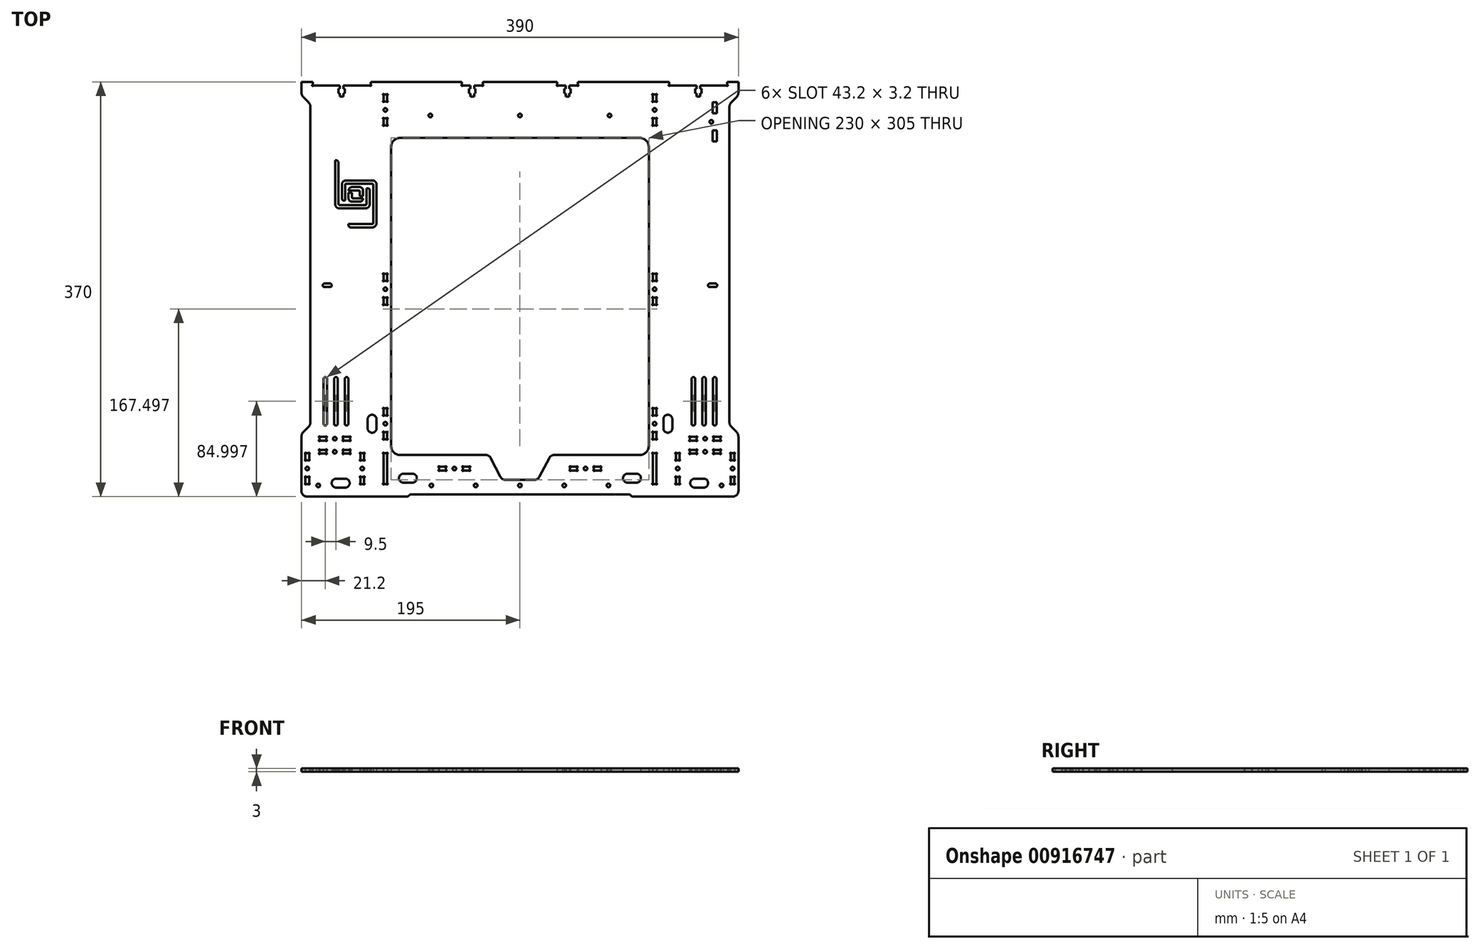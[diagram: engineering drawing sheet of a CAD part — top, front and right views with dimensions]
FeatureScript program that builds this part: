
annotation { "Feature Type Name" : "Feature", "Feature Type Description" : "" }
export const myFeature = defineFeature(function(context is Context, id is Id, definition is map)
    precondition{}
    {
        {
            var Q0;
            Q0=qCreatedBy(makeId("Top.planeOp"),FACE);
            var sketch = newSketch(context, id + "F0", { "sketchPlane" : qUnion([Q0])});
            skCircle(sketch, "E0", {"center": v(-180, -171.15) * mm, "radius": 1.6 * mm});
            skCircle(sketch, "E1", {"center": v(0, 158.85) * mm, "radius": 1.6 * mm});
            skLineSegment(sketch, "E2", {"start": v(-156, -165.15) * mm, "end": v(-164, -165.15) * mm});
            skArc(sketch, "E3", {"start": v(-156, -173.15) * mm, "mid": v(-152, -169.15) * mm, "end": v(-156, -165.15) * mm});
            skLineSegment(sketch, "E4", {"start": v(-164, -173.15) * mm, "end": v(-156, -173.15) * mm});
            skArc(sketch, "E5", {"start": v(-164, -165.15) * mm, "mid": v(-168, -169.15) * mm, "end": v(-164, -173.15) * mm});
            skLineSegment(sketch, "E6", {"start": v(156, -173.15) * mm, "end": v(164, -173.15) * mm});
            skArc(sketch, "E7", {"start": v(156, -165.15) * mm, "mid": v(152, -169.15) * mm, "end": v(156, -173.15) * mm});
            skLineSegment(sketch, "E8", {"start": v(164, -165.15) * mm, "end": v(156, -165.15) * mm});
            skArc(sketch, "E9", {"start": v(164, -173.15) * mm, "mid": v(168, -169.15) * mm, "end": v(164, -165.15) * mm});
            skLineSegment(sketch, "E10", {"start": v(-165.9, -76.15) * mm, "end": v(-165.9, -116.15) * mm});
            skArc(sketch, "E11", {"start": v(-162.7, -76.15) * mm, "mid": v(-164.3, -74.55) * mm, "end": v(-165.9, -76.15) * mm});
            skLineSegment(sketch, "E12", {"start": v(-162.7, -116.15) * mm, "end": v(-162.7, -76.15) * mm});
            skArc(sketch, "E13", {"start": v(-165.9, -116.15) * mm, "mid": v(-164.3, -117.75) * mm, "end": v(-162.7, -116.15) * mm});
            skLineSegment(sketch, "E14", {"start": v(-156.4, -76.15) * mm, "end": v(-156.4, -116.15) * mm});
            skArc(sketch, "E15", {"start": v(-153.2, -76.15) * mm, "mid": v(-154.8, -74.55) * mm, "end": v(-156.4, -76.15) * mm});
            skLineSegment(sketch, "E16", {"start": v(-153.2, -116.15) * mm, "end": v(-153.2, -76.15) * mm});
            skArc(sketch, "E17", {"start": v(-156.4, -116.15) * mm, "mid": v(-154.8, -117.75) * mm, "end": v(-153.2, -116.15) * mm});
            skLineSegment(sketch, "E18", {"start": v(-175.4, -76.15) * mm, "end": v(-175.4, -116.15) * mm});
            skArc(sketch, "E19", {"start": v(-172.2, -76.15) * mm, "mid": v(-173.8, -74.55) * mm, "end": v(-175.4, -76.15) * mm});
            skLineSegment(sketch, "E20", {"start": v(-172.2, -116.15) * mm, "end": v(-172.2, -76.15) * mm});
            skArc(sketch, "E21", {"start": v(-175.4, -116.15) * mm, "mid": v(-173.8, -117.75) * mm, "end": v(-172.2, -116.15) * mm});
            skCircle(sketch, "E22", {"center": v(170.82, 153.25) * mm, "radius": 1.6 * mm});
            skCircle(sketch, "E23", {"center": v(165.3, -141.15) * mm, "radius": 1.6 * mm});
            skLineSegment(sketch, "E24", {"start": v(-157.8, -140.37) * mm, "end": v(-157.8, -141.94) * mm});
            skArc(sketch, "E25", {"start": v(-157.8, -140.37) * mm, "mid": v(-157.87, -140.12) * mm, "end": v(-158.05, -139.94) * mm});
            skArc(sketch, "E26", {"start": v(-157.37, -139.25) * mm, "mid": v(-158.15, -139.15) * mm, "end": v(-158.05, -139.94) * mm});
            skArc(sketch, "E27", {"start": v(-157.37, -139.25) * mm, "mid": v(-157.18, -139.44) * mm, "end": v(-156.93, -139.5) * mm});
            skLineSegment(sketch, "E28", {"start": v(-152.47, -139.5) * mm, "end": v(-156.93, -139.5) * mm});
            skArc(sketch, "E29", {"start": v(-152.47, -139.5) * mm, "mid": v(-152.22, -139.44) * mm, "end": v(-152.03, -139.25) * mm});
            skArc(sketch, "E30", {"start": v(-151.35, -139.94) * mm, "mid": v(-151.25, -139.15) * mm, "end": v(-152.03, -139.25) * mm});
            skArc(sketch, "E31", {"start": v(-151.35, -139.94) * mm, "mid": v(-151.53, -140.12) * mm, "end": v(-151.6, -140.37) * mm});
            skLineSegment(sketch, "E32", {"start": v(-151.6, -141.94) * mm, "end": v(-151.6, -140.37) * mm});
            skArc(sketch, "E33", {"start": v(-151.6, -141.94) * mm, "mid": v(-151.53, -142.19) * mm, "end": v(-151.35, -142.37) * mm});
            skArc(sketch, "E34", {"start": v(-152.03, -143.05) * mm, "mid": v(-151.25, -143.16) * mm, "end": v(-151.35, -142.37) * mm});
            skArc(sketch, "E35", {"start": v(-152.03, -143.05) * mm, "mid": v(-152.22, -142.87) * mm, "end": v(-152.47, -142.8) * mm});
            skLineSegment(sketch, "E36", {"start": v(-156.93, -142.8) * mm, "end": v(-152.47, -142.8) * mm});
            skArc(sketch, "E37", {"start": v(-156.93, -142.8) * mm, "mid": v(-157.18, -142.87) * mm, "end": v(-157.37, -143.05) * mm});
            skArc(sketch, "E38", {"start": v(-158.05, -142.37) * mm, "mid": v(-158.15, -143.16) * mm, "end": v(-157.37, -143.05) * mm});
            skArc(sketch, "E39", {"start": v(-158.05, -142.37) * mm, "mid": v(-157.87, -142.19) * mm, "end": v(-157.8, -141.94) * mm});
            skLineSegment(sketch, "E40", {"start": v(-179, -140.37) * mm, "end": v(-179, -141.94) * mm});
            skArc(sketch, "E41", {"start": v(-179, -140.37) * mm, "mid": v(-179.07, -140.12) * mm, "end": v(-179.25, -139.94) * mm});
            skArc(sketch, "E42", {"start": v(-178.57, -139.25) * mm, "mid": v(-179.35, -139.15) * mm, "end": v(-179.25, -139.94) * mm});
            skArc(sketch, "E43", {"start": v(-178.57, -139.25) * mm, "mid": v(-178.38, -139.44) * mm, "end": v(-178.13, -139.5) * mm});
            skLineSegment(sketch, "E44", {"start": v(-173.67, -139.5) * mm, "end": v(-178.13, -139.5) * mm});
            skArc(sketch, "E45", {"start": v(-173.67, -139.5) * mm, "mid": v(-173.42, -139.44) * mm, "end": v(-173.23, -139.25) * mm});
            skArc(sketch, "E46", {"start": v(-172.55, -139.94) * mm, "mid": v(-172.45, -139.15) * mm, "end": v(-173.23, -139.25) * mm});
            skArc(sketch, "E47", {"start": v(-172.55, -139.94) * mm, "mid": v(-172.73, -140.12) * mm, "end": v(-172.8, -140.37) * mm});
            skLineSegment(sketch, "E48", {"start": v(-172.8, -141.94) * mm, "end": v(-172.8, -140.37) * mm});
            skArc(sketch, "E49", {"start": v(-172.8, -141.94) * mm, "mid": v(-172.73, -142.19) * mm, "end": v(-172.55, -142.37) * mm});
            skArc(sketch, "E50", {"start": v(-173.23, -143.05) * mm, "mid": v(-172.45, -143.16) * mm, "end": v(-172.55, -142.37) * mm});
            skArc(sketch, "E51", {"start": v(-173.23, -143.05) * mm, "mid": v(-173.42, -142.87) * mm, "end": v(-173.67, -142.8) * mm});
            skLineSegment(sketch, "E52", {"start": v(-178.13, -142.8) * mm, "end": v(-173.67, -142.8) * mm});
            skArc(sketch, "E53", {"start": v(-178.13, -142.8) * mm, "mid": v(-178.38, -142.87) * mm, "end": v(-178.57, -143.05) * mm});
            skArc(sketch, "E54", {"start": v(-179.25, -142.37) * mm, "mid": v(-179.35, -143.16) * mm, "end": v(-178.57, -143.05) * mm});
            skArc(sketch, "E55", {"start": v(-179.25, -142.37) * mm, "mid": v(-179.07, -142.19) * mm, "end": v(-179, -141.94) * mm});
            skLineSegment(sketch, "E56", {"start": v(-96, -160.75) * mm, "end": v(-104, -160.75) * mm});
            skArc(sketch, "E57", {"start": v(-96, -168.75) * mm, "mid": v(-92, -164.75) * mm, "end": v(-96, -160.75) * mm});
            skLineSegment(sketch, "E58", {"start": v(-104, -168.75) * mm, "end": v(-96, -168.75) * mm});
            skArc(sketch, "E59", {"start": v(-104, -160.75) * mm, "mid": v(-108, -164.75) * mm, "end": v(-104, -168.75) * mm});
            skLineSegment(sketch, "E60", {"start": v(104, -160.75) * mm, "end": v(96, -160.75) * mm});
            skArc(sketch, "E61", {"start": v(104, -168.75) * mm, "mid": v(108, -164.75) * mm, "end": v(104, -160.75) * mm});
            skLineSegment(sketch, "E62", {"start": v(96, -168.75) * mm, "end": v(104, -168.75) * mm});
            skArc(sketch, "E63", {"start": v(96, -160.75) * mm, "mid": v(92, -164.75) * mm, "end": v(96, -168.75) * mm});
            skCircle(sketch, "E64", {"center": v(-79.02, -171.15) * mm, "radius": 1.6 * mm});
            skCircle(sketch, "E65", {"center": v(39.5, -171.15) * mm, "radius": 1.6 * mm});
            skCircle(sketch, "E66", {"center": v(58.53, -156.15) * mm, "radius": 1.6 * mm});
            skLineSegment(sketch, "E67", {"start": v(-51.03, -155.37) * mm, "end": v(-51.03, -156.94) * mm});
            skArc(sketch, "E68", {"start": v(-51.03, -155.37) * mm, "mid": v(-51.1, -155.12) * mm, "end": v(-51.28, -154.94) * mm});
            skArc(sketch, "E69", {"start": v(-50.6, -154.25) * mm, "mid": v(-51.38, -154.15) * mm, "end": v(-51.28, -154.94) * mm});
            skArc(sketch, "E70", {"start": v(-50.6, -154.25) * mm, "mid": v(-50.4, -154.44) * mm, "end": v(-50.16, -154.5) * mm});
            skLineSegment(sketch, "E71", {"start": v(-45.7, -154.5) * mm, "end": v(-50.16, -154.5) * mm});
            skArc(sketch, "E72", {"start": v(-45.7, -154.5) * mm, "mid": v(-45.44, -154.44) * mm, "end": v(-45.26, -154.25) * mm});
            skArc(sketch, "E73", {"start": v(-44.58, -154.94) * mm, "mid": v(-44.47, -154.15) * mm, "end": v(-45.26, -154.25) * mm});
            skArc(sketch, "E74", {"start": v(-44.58, -154.94) * mm, "mid": v(-44.76, -155.12) * mm, "end": v(-44.83, -155.37) * mm});
            skLineSegment(sketch, "E75", {"start": v(-44.83, -156.94) * mm, "end": v(-44.83, -155.37) * mm});
            skArc(sketch, "E76", {"start": v(-44.83, -156.94) * mm, "mid": v(-44.76, -157.19) * mm, "end": v(-44.58, -157.37) * mm});
            skArc(sketch, "E77", {"start": v(-45.26, -158.05) * mm, "mid": v(-44.47, -158.16) * mm, "end": v(-44.58, -157.37) * mm});
            skArc(sketch, "E78", {"start": v(-45.26, -158.05) * mm, "mid": v(-45.44, -157.87) * mm, "end": v(-45.7, -157.8) * mm});
            skLineSegment(sketch, "E79", {"start": v(-50.16, -157.8) * mm, "end": v(-45.7, -157.8) * mm});
            skArc(sketch, "E80", {"start": v(-50.16, -157.8) * mm, "mid": v(-50.4, -157.87) * mm, "end": v(-50.6, -158.05) * mm});
            skArc(sketch, "E81", {"start": v(-51.28, -157.37) * mm, "mid": v(-51.38, -158.16) * mm, "end": v(-50.6, -158.05) * mm});
            skArc(sketch, "E82", {"start": v(-51.28, -157.37) * mm, "mid": v(-51.1, -157.19) * mm, "end": v(-51.03, -156.94) * mm});
            skLineSegment(sketch, "E83", {"start": v(-72.23, -155.37) * mm, "end": v(-72.23, -156.94) * mm});
            skArc(sketch, "E84", {"start": v(-72.23, -155.37) * mm, "mid": v(-72.3, -155.12) * mm, "end": v(-72.48, -154.94) * mm});
            skArc(sketch, "E85", {"start": v(-71.8, -154.25) * mm, "mid": v(-72.58, -154.15) * mm, "end": v(-72.48, -154.94) * mm});
            skArc(sketch, "E86", {"start": v(-71.8, -154.25) * mm, "mid": v(-71.6, -154.44) * mm, "end": v(-71.36, -154.5) * mm});
            skLineSegment(sketch, "E87", {"start": v(-66.9, -154.5) * mm, "end": v(-71.36, -154.5) * mm});
            skArc(sketch, "E88", {"start": v(-66.9, -154.5) * mm, "mid": v(-66.64, -154.44) * mm, "end": v(-66.46, -154.25) * mm});
            skArc(sketch, "E89", {"start": v(-65.78, -154.94) * mm, "mid": v(-65.67, -154.15) * mm, "end": v(-66.46, -154.25) * mm});
            skArc(sketch, "E90", {"start": v(-65.78, -154.94) * mm, "mid": v(-65.96, -155.12) * mm, "end": v(-66.03, -155.37) * mm});
            skLineSegment(sketch, "E91", {"start": v(-66.03, -156.94) * mm, "end": v(-66.03, -155.37) * mm});
            skArc(sketch, "E92", {"start": v(-66.03, -156.94) * mm, "mid": v(-65.96, -157.19) * mm, "end": v(-65.78, -157.37) * mm});
            skArc(sketch, "E93", {"start": v(-66.46, -158.05) * mm, "mid": v(-65.67, -158.16) * mm, "end": v(-65.78, -157.37) * mm});
            skArc(sketch, "E94", {"start": v(-66.46, -158.05) * mm, "mid": v(-66.64, -157.87) * mm, "end": v(-66.9, -157.8) * mm});
            skLineSegment(sketch, "E95", {"start": v(-71.36, -157.8) * mm, "end": v(-66.9, -157.8) * mm});
            skArc(sketch, "E96", {"start": v(-71.36, -157.8) * mm, "mid": v(-71.6, -157.87) * mm, "end": v(-71.8, -158.05) * mm});
            skArc(sketch, "E97", {"start": v(-72.48, -157.37) * mm, "mid": v(-72.58, -158.16) * mm, "end": v(-71.8, -158.05) * mm});
            skArc(sketch, "E98", {"start": v(-72.48, -157.37) * mm, "mid": v(-72.3, -157.19) * mm, "end": v(-72.23, -156.94) * mm});
            skCircle(sketch, "E99", {"center": v(189.82, -156.15) * mm, "radius": 1.6 * mm});
            skCircle(sketch, "E100", {"center": v(140.78, -156.15) * mm, "radius": 1.6 * mm});
            skCircle(sketch, "E101", {"center": v(120.17, 3.85) * mm, "radius": 1.6 * mm});
            skCircle(sketch, "E102", {"center": v(-120.18, 163.85) * mm, "radius": 1.6 * mm});
            skCircle(sketch, "E103", {"center": v(-120.17, -116.15) * mm, "radius": 1.6 * mm});
            skCircle(sketch, "E104", {"center": v(-165.3, -129.5) * mm, "radius": 1.6 * mm});
            skArc(sketch, "E105", {"start": v(188.17, -143.32) * mm, "mid": v(188.1, -143.07) * mm, "end": v(187.92, -142.89) * mm});
            skArc(sketch, "E106", {"start": v(188.6, -142.2) * mm, "mid": v(187.82, -142.1) * mm, "end": v(187.92, -142.89) * mm});
            skArc(sketch, "E107", {"start": v(188.6, -142.2) * mm, "mid": v(188.79, -142.39) * mm, "end": v(189.04, -142.45) * mm});
            skLineSegment(sketch, "E108", {"start": v(190.6, -142.45) * mm, "end": v(189.04, -142.45) * mm});
            skArc(sketch, "E109", {"start": v(190.6, -142.45) * mm, "mid": v(190.85, -142.39) * mm, "end": v(191.04, -142.2) * mm});
            skArc(sketch, "E110", {"start": v(191.72, -142.89) * mm, "mid": v(191.82, -142.1) * mm, "end": v(191.04, -142.2) * mm});
            skArc(sketch, "E111", {"start": v(191.72, -142.89) * mm, "mid": v(191.54, -143.07) * mm, "end": v(191.47, -143.32) * mm});
            skLineSegment(sketch, "E112", {"start": v(191.47, -147.79) * mm, "end": v(191.47, -143.32) * mm});
            skArc(sketch, "E113", {"start": v(191.47, -147.79) * mm, "mid": v(191.54, -148.04) * mm, "end": v(191.72, -148.22) * mm});
            skArc(sketch, "E114", {"start": v(191.04, -148.9) * mm, "mid": v(191.82, -149) * mm, "end": v(191.72, -148.22) * mm});
            skArc(sketch, "E115", {"start": v(191.04, -148.9) * mm, "mid": v(190.85, -148.72) * mm, "end": v(190.6, -148.65) * mm});
            skLineSegment(sketch, "E116", {"start": v(189.04, -148.65) * mm, "end": v(190.6, -148.65) * mm});
            skArc(sketch, "E117", {"start": v(189.04, -148.65) * mm, "mid": v(188.79, -148.72) * mm, "end": v(188.6, -148.9) * mm});
            skArc(sketch, "E118", {"start": v(187.92, -148.22) * mm, "mid": v(187.82, -149) * mm, "end": v(188.6, -148.9) * mm});
            skArc(sketch, "E119", {"start": v(187.92, -148.22) * mm, "mid": v(188.1, -148.04) * mm, "end": v(188.17, -147.79) * mm});
            skLineSegment(sketch, "E120", {"start": v(188.17, -143.32) * mm, "end": v(188.17, -147.79) * mm});
            skArc(sketch, "E121", {"start": v(188.17, -164.52) * mm, "mid": v(188.1, -164.27) * mm, "end": v(187.92, -164.09) * mm});
            skArc(sketch, "E122", {"start": v(188.6, -163.4) * mm, "mid": v(187.82, -163.3) * mm, "end": v(187.92, -164.09) * mm});
            skArc(sketch, "E123", {"start": v(188.6, -163.4) * mm, "mid": v(188.79, -163.59) * mm, "end": v(189.04, -163.65) * mm});
            skLineSegment(sketch, "E124", {"start": v(190.6, -163.65) * mm, "end": v(189.04, -163.65) * mm});
            skArc(sketch, "E125", {"start": v(190.6, -163.65) * mm, "mid": v(190.85, -163.59) * mm, "end": v(191.04, -163.4) * mm});
            skArc(sketch, "E126", {"start": v(191.72, -164.09) * mm, "mid": v(191.82, -163.3) * mm, "end": v(191.04, -163.4) * mm});
            skArc(sketch, "E127", {"start": v(191.72, -164.09) * mm, "mid": v(191.54, -164.27) * mm, "end": v(191.47, -164.52) * mm});
            skLineSegment(sketch, "E128", {"start": v(191.47, -168.99) * mm, "end": v(191.47, -164.52) * mm});
            skArc(sketch, "E129", {"start": v(191.47, -168.99) * mm, "mid": v(191.54, -169.24) * mm, "end": v(191.72, -169.42) * mm});
            skArc(sketch, "E130", {"start": v(191.04, -170.1) * mm, "mid": v(191.82, -170.2) * mm, "end": v(191.72, -169.42) * mm});
            skArc(sketch, "E131", {"start": v(191.04, -170.1) * mm, "mid": v(190.85, -169.92) * mm, "end": v(190.6, -169.85) * mm});
            skLineSegment(sketch, "E132", {"start": v(189.04, -169.85) * mm, "end": v(190.6, -169.85) * mm});
            skArc(sketch, "E133", {"start": v(189.04, -169.85) * mm, "mid": v(188.79, -169.92) * mm, "end": v(188.6, -170.1) * mm});
            skArc(sketch, "E134", {"start": v(187.92, -169.42) * mm, "mid": v(187.82, -170.2) * mm, "end": v(188.6, -170.1) * mm});
            skArc(sketch, "E135", {"start": v(187.92, -169.42) * mm, "mid": v(188.1, -169.24) * mm, "end": v(188.17, -168.99) * mm});
            skLineSegment(sketch, "E136", {"start": v(188.17, -164.52) * mm, "end": v(188.17, -168.99) * mm});
            skArc(sketch, "E137", {"start": v(178.13, -127.86) * mm, "mid": v(178.38, -127.8) * mm, "end": v(178.57, -127.6) * mm});
            skArc(sketch, "E138", {"start": v(179.25, -128.3) * mm, "mid": v(179.35, -127.5) * mm, "end": v(178.57, -127.6) * mm});
            skArc(sketch, "E139", {"start": v(179.25, -128.3) * mm, "mid": v(179.07, -128.47) * mm, "end": v(179, -128.72) * mm});
            skLineSegment(sketch, "E140", {"start": v(179, -130.3) * mm, "end": v(179, -128.72) * mm});
            skArc(sketch, "E141", {"start": v(179, -130.3) * mm, "mid": v(179.07, -130.54) * mm, "end": v(179.25, -130.72) * mm});
            skArc(sketch, "E142", {"start": v(178.57, -131.4) * mm, "mid": v(179.35, -131.51) * mm, "end": v(179.25, -130.72) * mm});
            skArc(sketch, "E143", {"start": v(178.57, -131.4) * mm, "mid": v(178.38, -131.22) * mm, "end": v(178.13, -131.16) * mm});
            skLineSegment(sketch, "E144", {"start": v(173.67, -131.16) * mm, "end": v(178.13, -131.16) * mm});
            skArc(sketch, "E145", {"start": v(173.67, -131.16) * mm, "mid": v(173.42, -131.22) * mm, "end": v(173.23, -131.4) * mm});
            skArc(sketch, "E146", {"start": v(172.55, -130.72) * mm, "mid": v(172.45, -131.51) * mm, "end": v(173.23, -131.4) * mm});
            skArc(sketch, "E147", {"start": v(172.55, -130.72) * mm, "mid": v(172.73, -130.54) * mm, "end": v(172.8, -130.3) * mm});
            skLineSegment(sketch, "E148", {"start": v(172.8, -128.72) * mm, "end": v(172.8, -130.3) * mm});
            skArc(sketch, "E149", {"start": v(172.8, -128.72) * mm, "mid": v(172.73, -128.47) * mm, "end": v(172.55, -128.3) * mm});
            skArc(sketch, "E150", {"start": v(173.23, -127.6) * mm, "mid": v(172.45, -127.5) * mm, "end": v(172.55, -128.3) * mm});
            skArc(sketch, "E151", {"start": v(173.23, -127.6) * mm, "mid": v(173.42, -127.8) * mm, "end": v(173.67, -127.86) * mm});
            skLineSegment(sketch, "E152", {"start": v(178.13, -127.86) * mm, "end": v(173.67, -127.86) * mm});
            skArc(sketch, "E153", {"start": v(156.93, -127.86) * mm, "mid": v(157.18, -127.8) * mm, "end": v(157.37, -127.6) * mm});
            skArc(sketch, "E154", {"start": v(158.05, -128.3) * mm, "mid": v(158.15, -127.5) * mm, "end": v(157.37, -127.6) * mm});
            skArc(sketch, "E155", {"start": v(158.05, -128.3) * mm, "mid": v(157.87, -128.47) * mm, "end": v(157.8, -128.72) * mm});
            skLineSegment(sketch, "E156", {"start": v(157.8, -130.3) * mm, "end": v(157.8, -128.72) * mm});
            skArc(sketch, "E157", {"start": v(157.8, -130.3) * mm, "mid": v(157.87, -130.54) * mm, "end": v(158.05, -130.72) * mm});
            skArc(sketch, "E158", {"start": v(157.37, -131.4) * mm, "mid": v(158.15, -131.51) * mm, "end": v(158.05, -130.72) * mm});
            skArc(sketch, "E159", {"start": v(157.37, -131.4) * mm, "mid": v(157.18, -131.22) * mm, "end": v(156.93, -131.16) * mm});
            skLineSegment(sketch, "E160", {"start": v(152.47, -131.16) * mm, "end": v(156.93, -131.16) * mm});
            skArc(sketch, "E161", {"start": v(152.47, -131.16) * mm, "mid": v(152.22, -131.22) * mm, "end": v(152.03, -131.4) * mm});
            skArc(sketch, "E162", {"start": v(151.35, -130.72) * mm, "mid": v(151.25, -131.51) * mm, "end": v(152.03, -131.4) * mm});
            skArc(sketch, "E163", {"start": v(151.35, -130.72) * mm, "mid": v(151.53, -130.54) * mm, "end": v(151.6, -130.3) * mm});
            skLineSegment(sketch, "E164", {"start": v(151.6, -128.72) * mm, "end": v(151.6, -130.3) * mm});
            skArc(sketch, "E165", {"start": v(151.6, -128.72) * mm, "mid": v(151.53, -128.47) * mm, "end": v(151.35, -128.3) * mm});
            skArc(sketch, "E166", {"start": v(152.03, -127.6) * mm, "mid": v(151.25, -127.5) * mm, "end": v(151.35, -128.3) * mm});
            skArc(sketch, "E167", {"start": v(152.03, -127.6) * mm, "mid": v(152.22, -127.8) * mm, "end": v(152.47, -127.86) * mm});
            skLineSegment(sketch, "E168", {"start": v(156.93, -127.86) * mm, "end": v(152.47, -127.86) * mm});
            skArc(sketch, "E169", {"start": v(139.13, -143.32) * mm, "mid": v(139.06, -143.07) * mm, "end": v(138.88, -142.89) * mm});
            skArc(sketch, "E170", {"start": v(139.56, -142.2) * mm, "mid": v(138.78, -142.1) * mm, "end": v(138.88, -142.89) * mm});
            skArc(sketch, "E171", {"start": v(139.56, -142.2) * mm, "mid": v(139.75, -142.39) * mm, "end": v(140, -142.45) * mm});
            skLineSegment(sketch, "E172", {"start": v(141.56, -142.45) * mm, "end": v(140, -142.45) * mm});
            skArc(sketch, "E173", {"start": v(141.56, -142.45) * mm, "mid": v(141.81, -142.39) * mm, "end": v(142, -142.2) * mm});
            skArc(sketch, "E174", {"start": v(142.68, -142.89) * mm, "mid": v(142.78, -142.1) * mm, "end": v(142, -142.2) * mm});
            skArc(sketch, "E175", {"start": v(142.68, -142.89) * mm, "mid": v(142.5, -143.07) * mm, "end": v(142.43, -143.32) * mm});
            skLineSegment(sketch, "E176", {"start": v(142.43, -147.79) * mm, "end": v(142.43, -143.32) * mm});
            skArc(sketch, "E177", {"start": v(142.43, -147.79) * mm, "mid": v(142.5, -148.04) * mm, "end": v(142.68, -148.22) * mm});
            skArc(sketch, "E178", {"start": v(142, -148.9) * mm, "mid": v(142.78, -149) * mm, "end": v(142.68, -148.22) * mm});
            skArc(sketch, "E179", {"start": v(142, -148.9) * mm, "mid": v(141.81, -148.72) * mm, "end": v(141.56, -148.65) * mm});
            skLineSegment(sketch, "E180", {"start": v(140, -148.65) * mm, "end": v(141.56, -148.65) * mm});
            skArc(sketch, "E181", {"start": v(140, -148.65) * mm, "mid": v(139.75, -148.72) * mm, "end": v(139.56, -148.9) * mm});
            skArc(sketch, "E182", {"start": v(138.88, -148.22) * mm, "mid": v(138.78, -149) * mm, "end": v(139.56, -148.9) * mm});
            skArc(sketch, "E183", {"start": v(138.88, -148.22) * mm, "mid": v(139.06, -148.04) * mm, "end": v(139.13, -147.79) * mm});
            skLineSegment(sketch, "E184", {"start": v(139.13, -143.32) * mm, "end": v(139.13, -147.79) * mm});
            skArc(sketch, "E185", {"start": v(139.13, -164.52) * mm, "mid": v(139.06, -164.27) * mm, "end": v(138.88, -164.09) * mm});
            skArc(sketch, "E186", {"start": v(139.56, -163.4) * mm, "mid": v(138.78, -163.3) * mm, "end": v(138.88, -164.09) * mm});
            skArc(sketch, "E187", {"start": v(139.56, -163.4) * mm, "mid": v(139.75, -163.59) * mm, "end": v(140, -163.65) * mm});
            skLineSegment(sketch, "E188", {"start": v(141.56, -163.65) * mm, "end": v(140, -163.65) * mm});
            skArc(sketch, "E189", {"start": v(141.56, -163.65) * mm, "mid": v(141.81, -163.59) * mm, "end": v(142, -163.4) * mm});
            skArc(sketch, "E190", {"start": v(142.68, -164.09) * mm, "mid": v(142.78, -163.3) * mm, "end": v(142, -163.4) * mm});
            skArc(sketch, "E191", {"start": v(142.68, -164.09) * mm, "mid": v(142.5, -164.27) * mm, "end": v(142.43, -164.52) * mm});
            skLineSegment(sketch, "E192", {"start": v(142.43, -168.99) * mm, "end": v(142.43, -164.52) * mm});
            skArc(sketch, "E193", {"start": v(142.43, -168.99) * mm, "mid": v(142.5, -169.24) * mm, "end": v(142.68, -169.42) * mm});
            skArc(sketch, "E194", {"start": v(142, -170.1) * mm, "mid": v(142.78, -170.2) * mm, "end": v(142.68, -169.42) * mm});
            skArc(sketch, "E195", {"start": v(142, -170.1) * mm, "mid": v(141.81, -169.92) * mm, "end": v(141.56, -169.85) * mm});
            skLineSegment(sketch, "E196", {"start": v(140, -169.85) * mm, "end": v(141.56, -169.85) * mm});
            skArc(sketch, "E197", {"start": v(140, -169.85) * mm, "mid": v(139.75, -169.92) * mm, "end": v(139.56, -170.1) * mm});
            skArc(sketch, "E198", {"start": v(138.88, -169.42) * mm, "mid": v(138.78, -170.2) * mm, "end": v(139.56, -170.1) * mm});
            skArc(sketch, "E199", {"start": v(138.88, -169.42) * mm, "mid": v(139.06, -169.24) * mm, "end": v(139.13, -168.99) * mm});
            skLineSegment(sketch, "E200", {"start": v(139.13, -164.52) * mm, "end": v(139.13, -168.99) * mm});
            skLineSegment(sketch, "E201", {"start": v(120.96, 177.55) * mm, "end": v(119.4, 177.55) * mm});
            skArc(sketch, "E202", {"start": v(120.96, 177.55) * mm, "mid": v(121.2, 177.61) * mm, "end": v(121.4, 177.8) * mm});
            skArc(sketch, "E203", {"start": v(122.07, 177.11) * mm, "mid": v(122.18, 177.9) * mm, "end": v(121.4, 177.8) * mm});
            skArc(sketch, "E204", {"start": v(122.07, 177.11) * mm, "mid": v(121.9, 176.93) * mm, "end": v(121.82, 176.68) * mm});
            skLineSegment(sketch, "E205", {"start": v(121.82, 172.21) * mm, "end": v(121.82, 176.68) * mm});
            skArc(sketch, "E206", {"start": v(121.82, 172.21) * mm, "mid": v(121.9, 171.96) * mm, "end": v(122.07, 171.78) * mm});
            skArc(sketch, "E207", {"start": v(121.4, 171.1) * mm, "mid": v(122.18, 171) * mm, "end": v(122.07, 171.78) * mm});
            skArc(sketch, "E208", {"start": v(121.4, 171.1) * mm, "mid": v(121.2, 171.28) * mm, "end": v(120.96, 171.35) * mm});
            skLineSegment(sketch, "E209", {"start": v(119.4, 171.35) * mm, "end": v(120.96, 171.35) * mm});
            skArc(sketch, "E210", {"start": v(119.4, 171.35) * mm, "mid": v(119.14, 171.28) * mm, "end": v(118.96, 171.1) * mm});
            skArc(sketch, "E211", {"start": v(118.28, 171.78) * mm, "mid": v(118.17, 171) * mm, "end": v(118.96, 171.1) * mm});
            skArc(sketch, "E212", {"start": v(118.28, 171.78) * mm, "mid": v(118.46, 171.96) * mm, "end": v(118.53, 172.21) * mm});
            skLineSegment(sketch, "E213", {"start": v(118.53, 176.68) * mm, "end": v(118.53, 172.21) * mm});
            skArc(sketch, "E214", {"start": v(118.53, 176.68) * mm, "mid": v(118.46, 176.93) * mm, "end": v(118.28, 177.11) * mm});
            skArc(sketch, "E215", {"start": v(118.96, 177.8) * mm, "mid": v(118.17, 177.9) * mm, "end": v(118.28, 177.11) * mm});
            skArc(sketch, "E216", {"start": v(118.96, 177.8) * mm, "mid": v(119.14, 177.61) * mm, "end": v(119.4, 177.55) * mm});
            skLineSegment(sketch, "E217", {"start": v(120.96, 156.35) * mm, "end": v(119.4, 156.35) * mm});
            skArc(sketch, "E218", {"start": v(120.96, 156.35) * mm, "mid": v(121.2, 156.41) * mm, "end": v(121.4, 156.6) * mm});
            skArc(sketch, "E219", {"start": v(122.07, 155.91) * mm, "mid": v(122.18, 156.7) * mm, "end": v(121.4, 156.6) * mm});
            skArc(sketch, "E220", {"start": v(122.07, 155.91) * mm, "mid": v(121.9, 155.73) * mm, "end": v(121.82, 155.48) * mm});
            skLineSegment(sketch, "E221", {"start": v(121.82, 151.01) * mm, "end": v(121.82, 155.48) * mm});
            skArc(sketch, "E222", {"start": v(121.82, 151.01) * mm, "mid": v(121.9, 150.76) * mm, "end": v(122.07, 150.58) * mm});
            skArc(sketch, "E223", {"start": v(121.4, 149.9) * mm, "mid": v(122.18, 149.8) * mm, "end": v(122.07, 150.58) * mm});
            skArc(sketch, "E224", {"start": v(121.4, 149.9) * mm, "mid": v(121.2, 150.08) * mm, "end": v(120.96, 150.15) * mm});
            skLineSegment(sketch, "E225", {"start": v(119.4, 150.15) * mm, "end": v(120.96, 150.15) * mm});
            skArc(sketch, "E226", {"start": v(119.4, 150.15) * mm, "mid": v(119.14, 150.08) * mm, "end": v(118.96, 149.9) * mm});
            skArc(sketch, "E227", {"start": v(118.28, 150.58) * mm, "mid": v(118.17, 149.8) * mm, "end": v(118.96, 149.9) * mm});
            skArc(sketch, "E228", {"start": v(118.28, 150.58) * mm, "mid": v(118.46, 150.76) * mm, "end": v(118.53, 151.01) * mm});
            skLineSegment(sketch, "E229", {"start": v(118.53, 155.48) * mm, "end": v(118.53, 151.01) * mm});
            skArc(sketch, "E230", {"start": v(118.53, 155.48) * mm, "mid": v(118.46, 155.73) * mm, "end": v(118.28, 155.91) * mm});
            skArc(sketch, "E231", {"start": v(118.96, 156.6) * mm, "mid": v(118.17, 156.7) * mm, "end": v(118.28, 155.91) * mm});
            skArc(sketch, "E232", {"start": v(118.96, 156.6) * mm, "mid": v(119.14, 156.41) * mm, "end": v(119.4, 156.35) * mm});
            skLineSegment(sketch, "E233", {"start": v(120.96, 17.55) * mm, "end": v(119.4, 17.55) * mm});
            skArc(sketch, "E234", {"start": v(120.96, 17.55) * mm, "mid": v(121.2, 17.61) * mm, "end": v(121.4, 17.8) * mm});
            skArc(sketch, "E235", {"start": v(122.07, 17.11) * mm, "mid": v(122.18, 17.9) * mm, "end": v(121.4, 17.8) * mm});
            skArc(sketch, "E236", {"start": v(122.07, 17.11) * mm, "mid": v(121.9, 16.93) * mm, "end": v(121.82, 16.68) * mm});
            skLineSegment(sketch, "E237", {"start": v(121.82, 12.21) * mm, "end": v(121.82, 16.68) * mm});
            skArc(sketch, "E238", {"start": v(121.82, 12.21) * mm, "mid": v(121.9, 11.96) * mm, "end": v(122.07, 11.78) * mm});
            skArc(sketch, "E239", {"start": v(121.4, 11.1) * mm, "mid": v(122.18, 11) * mm, "end": v(122.07, 11.78) * mm});
            skArc(sketch, "E240", {"start": v(121.4, 11.1) * mm, "mid": v(121.2, 11.28) * mm, "end": v(120.96, 11.35) * mm});
            skLineSegment(sketch, "E241", {"start": v(119.4, 11.35) * mm, "end": v(120.96, 11.35) * mm});
            skArc(sketch, "E242", {"start": v(119.4, 11.35) * mm, "mid": v(119.14, 11.28) * mm, "end": v(118.96, 11.1) * mm});
            skArc(sketch, "E243", {"start": v(118.28, 11.78) * mm, "mid": v(118.17, 11) * mm, "end": v(118.96, 11.1) * mm});
            skArc(sketch, "E244", {"start": v(118.28, 11.78) * mm, "mid": v(118.46, 11.96) * mm, "end": v(118.53, 12.21) * mm});
            skLineSegment(sketch, "E245", {"start": v(118.53, 16.68) * mm, "end": v(118.53, 12.21) * mm});
            skArc(sketch, "E246", {"start": v(118.53, 16.68) * mm, "mid": v(118.46, 16.93) * mm, "end": v(118.28, 17.11) * mm});
            skArc(sketch, "E247", {"start": v(118.96, 17.8) * mm, "mid": v(118.17, 17.9) * mm, "end": v(118.28, 17.11) * mm});
            skArc(sketch, "E248", {"start": v(118.96, 17.8) * mm, "mid": v(119.14, 17.61) * mm, "end": v(119.4, 17.55) * mm});
            skLineSegment(sketch, "E249", {"start": v(120.96, -3.65) * mm, "end": v(119.4, -3.65) * mm});
            skArc(sketch, "E250", {"start": v(120.96, -3.65) * mm, "mid": v(121.2, -3.59) * mm, "end": v(121.4, -3.4) * mm});
            skArc(sketch, "E251", {"start": v(122.07, -4.09) * mm, "mid": v(122.18, -3.3) * mm, "end": v(121.4, -3.4) * mm});
            skArc(sketch, "E252", {"start": v(122.07, -4.09) * mm, "mid": v(121.9, -4.27) * mm, "end": v(121.82, -4.52) * mm});
            skLineSegment(sketch, "E253", {"start": v(121.82, -8.99) * mm, "end": v(121.82, -4.52) * mm});
            skArc(sketch, "E254", {"start": v(121.82, -8.99) * mm, "mid": v(121.9, -9.24) * mm, "end": v(122.07, -9.42) * mm});
            skArc(sketch, "E255", {"start": v(121.4, -10.1) * mm, "mid": v(122.18, -10.2) * mm, "end": v(122.07, -9.42) * mm});
            skArc(sketch, "E256", {"start": v(121.4, -10.1) * mm, "mid": v(121.2, -9.92) * mm, "end": v(120.96, -9.85) * mm});
            skLineSegment(sketch, "E257", {"start": v(119.4, -9.85) * mm, "end": v(120.96, -9.85) * mm});
            skArc(sketch, "E258", {"start": v(119.4, -9.85) * mm, "mid": v(119.14, -9.92) * mm, "end": v(118.96, -10.1) * mm});
            skArc(sketch, "E259", {"start": v(118.28, -9.42) * mm, "mid": v(118.17, -10.2) * mm, "end": v(118.96, -10.1) * mm});
            skArc(sketch, "E260", {"start": v(118.28, -9.42) * mm, "mid": v(118.46, -9.24) * mm, "end": v(118.53, -8.99) * mm});
            skLineSegment(sketch, "E261", {"start": v(118.53, -4.52) * mm, "end": v(118.53, -8.99) * mm});
            skArc(sketch, "E262", {"start": v(118.53, -4.52) * mm, "mid": v(118.46, -4.27) * mm, "end": v(118.28, -4.09) * mm});
            skArc(sketch, "E263", {"start": v(118.96, -3.4) * mm, "mid": v(118.17, -3.3) * mm, "end": v(118.28, -4.09) * mm});
            skArc(sketch, "E264", {"start": v(118.96, -3.4) * mm, "mid": v(119.14, -3.59) * mm, "end": v(119.4, -3.65) * mm});
            skArc(sketch, "E265", {"start": v(118.53, -103.32) * mm, "mid": v(118.46, -103.07) * mm, "end": v(118.28, -102.89) * mm});
            skArc(sketch, "E266", {"start": v(118.96, -102.2) * mm, "mid": v(118.17, -102.1) * mm, "end": v(118.28, -102.89) * mm});
            skArc(sketch, "E267", {"start": v(118.96, -102.2) * mm, "mid": v(119.14, -102.39) * mm, "end": v(119.4, -102.45) * mm});
            skLineSegment(sketch, "E268", {"start": v(120.96, -102.45) * mm, "end": v(119.4, -102.45) * mm});
            skArc(sketch, "E269", {"start": v(120.96, -102.45) * mm, "mid": v(121.2, -102.39) * mm, "end": v(121.4, -102.2) * mm});
            skArc(sketch, "E270", {"start": v(122.07, -102.89) * mm, "mid": v(122.18, -102.1) * mm, "end": v(121.4, -102.2) * mm});
            skArc(sketch, "E271", {"start": v(122.07, -102.89) * mm, "mid": v(121.9, -103.07) * mm, "end": v(121.83, -103.32) * mm});
            skLineSegment(sketch, "E272", {"start": v(121.83, -107.79) * mm, "end": v(121.83, -103.32) * mm});
            skArc(sketch, "E273", {"start": v(121.83, -107.79) * mm, "mid": v(121.9, -108.04) * mm, "end": v(122.08, -108.22) * mm});
            skArc(sketch, "E274", {"start": v(121.4, -108.9) * mm, "mid": v(122.18, -109) * mm, "end": v(122.08, -108.22) * mm});
            skArc(sketch, "E275", {"start": v(121.4, -108.9) * mm, "mid": v(121.2, -108.72) * mm, "end": v(120.96, -108.65) * mm});
            skLineSegment(sketch, "E276", {"start": v(119.4, -108.65) * mm, "end": v(120.96, -108.65) * mm});
            skArc(sketch, "E277", {"start": v(119.4, -108.65) * mm, "mid": v(119.14, -108.72) * mm, "end": v(118.96, -108.9) * mm});
            skArc(sketch, "E278", {"start": v(118.28, -108.22) * mm, "mid": v(118.17, -109) * mm, "end": v(118.96, -108.9) * mm});
            skArc(sketch, "E279", {"start": v(118.28, -108.22) * mm, "mid": v(118.46, -108.04) * mm, "end": v(118.53, -107.79) * mm});
            skLineSegment(sketch, "E280", {"start": v(118.53, -103.32) * mm, "end": v(118.53, -107.79) * mm});
            skArc(sketch, "E281", {"start": v(118.53, -124.52) * mm, "mid": v(118.46, -124.27) * mm, "end": v(118.28, -124.09) * mm});
            skArc(sketch, "E282", {"start": v(118.96, -123.4) * mm, "mid": v(118.17, -123.3) * mm, "end": v(118.28, -124.09) * mm});
            skArc(sketch, "E283", {"start": v(118.96, -123.4) * mm, "mid": v(119.14, -123.59) * mm, "end": v(119.4, -123.65) * mm});
            skLineSegment(sketch, "E284", {"start": v(120.96, -123.65) * mm, "end": v(119.4, -123.65) * mm});
            skArc(sketch, "E285", {"start": v(120.96, -123.65) * mm, "mid": v(121.2, -123.59) * mm, "end": v(121.4, -123.4) * mm});
            skArc(sketch, "E286", {"start": v(122.07, -124.09) * mm, "mid": v(122.18, -123.3) * mm, "end": v(121.4, -123.4) * mm});
            skArc(sketch, "E287", {"start": v(122.07, -124.09) * mm, "mid": v(121.9, -124.27) * mm, "end": v(121.83, -124.52) * mm});
            skLineSegment(sketch, "E288", {"start": v(121.83, -128.99) * mm, "end": v(121.83, -124.52) * mm});
            skArc(sketch, "E289", {"start": v(121.83, -128.99) * mm, "mid": v(121.9, -129.24) * mm, "end": v(122.08, -129.42) * mm});
            skArc(sketch, "E290", {"start": v(121.4, -130.1) * mm, "mid": v(122.18, -130.2) * mm, "end": v(122.08, -129.42) * mm});
            skArc(sketch, "E291", {"start": v(121.4, -130.1) * mm, "mid": v(121.2, -129.92) * mm, "end": v(120.96, -129.85) * mm});
            skLineSegment(sketch, "E292", {"start": v(119.4, -129.85) * mm, "end": v(120.96, -129.85) * mm});
            skArc(sketch, "E293", {"start": v(119.4, -129.85) * mm, "mid": v(119.14, -129.92) * mm, "end": v(118.96, -130.1) * mm});
            skArc(sketch, "E294", {"start": v(118.28, -129.42) * mm, "mid": v(118.17, -130.2) * mm, "end": v(118.96, -130.1) * mm});
            skArc(sketch, "E295", {"start": v(118.28, -129.42) * mm, "mid": v(118.46, -129.24) * mm, "end": v(118.53, -128.99) * mm});
            skLineSegment(sketch, "E296", {"start": v(118.53, -124.52) * mm, "end": v(118.53, -128.99) * mm});
            skLineSegment(sketch, "E297", {"start": v(-119.4, 177.55) * mm, "end": v(-120.96, 177.55) * mm});
            skArc(sketch, "E298", {"start": v(-119.4, 177.55) * mm, "mid": v(-119.14, 177.61) * mm, "end": v(-118.96, 177.8) * mm});
            skArc(sketch, "E299", {"start": v(-118.28, 177.11) * mm, "mid": v(-118.17, 177.9) * mm, "end": v(-118.96, 177.8) * mm});
            skArc(sketch, "E300", {"start": v(-118.28, 177.11) * mm, "mid": v(-118.46, 176.93) * mm, "end": v(-118.53, 176.68) * mm});
            skLineSegment(sketch, "E301", {"start": v(-118.53, 172.21) * mm, "end": v(-118.53, 176.68) * mm});
            skArc(sketch, "E302", {"start": v(-118.53, 172.21) * mm, "mid": v(-118.46, 171.96) * mm, "end": v(-118.28, 171.78) * mm});
            skArc(sketch, "E303", {"start": v(-118.96, 171.1) * mm, "mid": v(-118.17, 171) * mm, "end": v(-118.28, 171.78) * mm});
            skArc(sketch, "E304", {"start": v(-118.96, 171.1) * mm, "mid": v(-119.14, 171.28) * mm, "end": v(-119.4, 171.35) * mm});
            skLineSegment(sketch, "E305", {"start": v(-120.96, 171.35) * mm, "end": v(-119.4, 171.35) * mm});
            skArc(sketch, "E306", {"start": v(-120.96, 171.35) * mm, "mid": v(-121.2, 171.28) * mm, "end": v(-121.4, 171.1) * mm});
            skArc(sketch, "E307", {"start": v(-122.07, 171.78) * mm, "mid": v(-122.18, 171) * mm, "end": v(-121.4, 171.1) * mm});
            skArc(sketch, "E308", {"start": v(-122.07, 171.78) * mm, "mid": v(-121.9, 171.96) * mm, "end": v(-121.82, 172.21) * mm});
            skLineSegment(sketch, "E309", {"start": v(-121.82, 176.68) * mm, "end": v(-121.82, 172.21) * mm});
            skArc(sketch, "E310", {"start": v(-121.82, 176.68) * mm, "mid": v(-121.9, 176.93) * mm, "end": v(-122.07, 177.11) * mm});
            skArc(sketch, "E311", {"start": v(-121.4, 177.8) * mm, "mid": v(-122.18, 177.9) * mm, "end": v(-122.07, 177.11) * mm});
            skArc(sketch, "E312", {"start": v(-121.4, 177.8) * mm, "mid": v(-121.2, 177.61) * mm, "end": v(-120.96, 177.55) * mm});
            skLineSegment(sketch, "E313", {"start": v(-119.4, 156.35) * mm, "end": v(-120.96, 156.35) * mm});
            skArc(sketch, "E314", {"start": v(-119.4, 156.35) * mm, "mid": v(-119.14, 156.41) * mm, "end": v(-118.96, 156.6) * mm});
            skArc(sketch, "E315", {"start": v(-118.28, 155.91) * mm, "mid": v(-118.17, 156.7) * mm, "end": v(-118.96, 156.6) * mm});
            skArc(sketch, "E316", {"start": v(-118.28, 155.91) * mm, "mid": v(-118.46, 155.73) * mm, "end": v(-118.53, 155.48) * mm});
            skLineSegment(sketch, "E317", {"start": v(-118.53, 151.01) * mm, "end": v(-118.53, 155.48) * mm});
            skArc(sketch, "E318", {"start": v(-118.53, 151.01) * mm, "mid": v(-118.46, 150.76) * mm, "end": v(-118.28, 150.58) * mm});
            skArc(sketch, "E319", {"start": v(-118.96, 149.9) * mm, "mid": v(-118.17, 149.8) * mm, "end": v(-118.28, 150.58) * mm});
            skArc(sketch, "E320", {"start": v(-118.96, 149.9) * mm, "mid": v(-119.14, 150.08) * mm, "end": v(-119.4, 150.15) * mm});
            skLineSegment(sketch, "E321", {"start": v(-120.96, 150.15) * mm, "end": v(-119.4, 150.15) * mm});
            skArc(sketch, "E322", {"start": v(-120.96, 150.15) * mm, "mid": v(-121.2, 150.08) * mm, "end": v(-121.4, 149.9) * mm});
            skArc(sketch, "E323", {"start": v(-122.07, 150.58) * mm, "mid": v(-122.18, 149.8) * mm, "end": v(-121.4, 149.9) * mm});
            skArc(sketch, "E324", {"start": v(-122.07, 150.58) * mm, "mid": v(-121.9, 150.76) * mm, "end": v(-121.82, 151.01) * mm});
            skLineSegment(sketch, "E325", {"start": v(-121.82, 155.48) * mm, "end": v(-121.82, 151.01) * mm});
            skArc(sketch, "E326", {"start": v(-121.82, 155.48) * mm, "mid": v(-121.9, 155.73) * mm, "end": v(-122.07, 155.91) * mm});
            skArc(sketch, "E327", {"start": v(-121.4, 156.6) * mm, "mid": v(-122.18, 156.7) * mm, "end": v(-122.07, 155.91) * mm});
            skArc(sketch, "E328", {"start": v(-121.4, 156.6) * mm, "mid": v(-121.2, 156.41) * mm, "end": v(-120.96, 156.35) * mm});
            skLineSegment(sketch, "E329", {"start": v(-119.4, 17.55) * mm, "end": v(-120.96, 17.55) * mm});
            skArc(sketch, "E330", {"start": v(-119.4, 17.55) * mm, "mid": v(-119.14, 17.61) * mm, "end": v(-118.96, 17.8) * mm});
            skArc(sketch, "E331", {"start": v(-118.28, 17.11) * mm, "mid": v(-118.17, 17.9) * mm, "end": v(-118.96, 17.8) * mm});
            skArc(sketch, "E332", {"start": v(-118.28, 17.11) * mm, "mid": v(-118.46, 16.93) * mm, "end": v(-118.53, 16.68) * mm});
            skLineSegment(sketch, "E333", {"start": v(-118.53, 12.21) * mm, "end": v(-118.53, 16.68) * mm});
            skArc(sketch, "E334", {"start": v(-118.53, 12.21) * mm, "mid": v(-118.46, 11.96) * mm, "end": v(-118.28, 11.78) * mm});
            skArc(sketch, "E335", {"start": v(-118.96, 11.1) * mm, "mid": v(-118.17, 11) * mm, "end": v(-118.28, 11.78) * mm});
            skArc(sketch, "E336", {"start": v(-118.96, 11.1) * mm, "mid": v(-119.14, 11.28) * mm, "end": v(-119.4, 11.35) * mm});
            skLineSegment(sketch, "E337", {"start": v(-120.96, 11.35) * mm, "end": v(-119.4, 11.35) * mm});
            skArc(sketch, "E338", {"start": v(-120.96, 11.35) * mm, "mid": v(-121.2, 11.28) * mm, "end": v(-121.4, 11.1) * mm});
            skArc(sketch, "E339", {"start": v(-122.07, 11.78) * mm, "mid": v(-122.18, 11) * mm, "end": v(-121.4, 11.1) * mm});
            skArc(sketch, "E340", {"start": v(-122.07, 11.78) * mm, "mid": v(-121.9, 11.96) * mm, "end": v(-121.82, 12.21) * mm});
            skLineSegment(sketch, "E341", {"start": v(-121.82, 16.68) * mm, "end": v(-121.82, 12.21) * mm});
            skArc(sketch, "E342", {"start": v(-121.82, 16.68) * mm, "mid": v(-121.9, 16.93) * mm, "end": v(-122.07, 17.11) * mm});
            skArc(sketch, "E343", {"start": v(-121.4, 17.8) * mm, "mid": v(-122.18, 17.9) * mm, "end": v(-122.07, 17.11) * mm});
            skArc(sketch, "E344", {"start": v(-121.4, 17.8) * mm, "mid": v(-121.2, 17.61) * mm, "end": v(-120.96, 17.55) * mm});
            skLineSegment(sketch, "E345", {"start": v(-119.4, -3.65) * mm, "end": v(-120.96, -3.65) * mm});
            skArc(sketch, "E346", {"start": v(-119.4, -3.65) * mm, "mid": v(-119.14, -3.59) * mm, "end": v(-118.96, -3.4) * mm});
            skArc(sketch, "E347", {"start": v(-118.28, -4.09) * mm, "mid": v(-118.17, -3.3) * mm, "end": v(-118.96, -3.4) * mm});
            skArc(sketch, "E348", {"start": v(-118.28, -4.09) * mm, "mid": v(-118.46, -4.27) * mm, "end": v(-118.53, -4.52) * mm});
            skLineSegment(sketch, "E349", {"start": v(-118.53, -8.99) * mm, "end": v(-118.53, -4.52) * mm});
            skArc(sketch, "E350", {"start": v(-118.53, -8.99) * mm, "mid": v(-118.46, -9.24) * mm, "end": v(-118.28, -9.42) * mm});
            skArc(sketch, "E351", {"start": v(-118.96, -10.1) * mm, "mid": v(-118.17, -10.2) * mm, "end": v(-118.28, -9.42) * mm});
            skArc(sketch, "E352", {"start": v(-118.96, -10.1) * mm, "mid": v(-119.14, -9.92) * mm, "end": v(-119.4, -9.85) * mm});
            skLineSegment(sketch, "E353", {"start": v(-120.96, -9.85) * mm, "end": v(-119.4, -9.85) * mm});
            skArc(sketch, "E354", {"start": v(-120.96, -9.85) * mm, "mid": v(-121.2, -9.92) * mm, "end": v(-121.4, -10.1) * mm});
            skArc(sketch, "E355", {"start": v(-122.07, -9.42) * mm, "mid": v(-122.18, -10.2) * mm, "end": v(-121.4, -10.1) * mm});
            skArc(sketch, "E356", {"start": v(-122.07, -9.42) * mm, "mid": v(-121.9, -9.24) * mm, "end": v(-121.82, -8.99) * mm});
            skLineSegment(sketch, "E357", {"start": v(-121.82, -4.52) * mm, "end": v(-121.82, -8.99) * mm});
            skArc(sketch, "E358", {"start": v(-121.82, -4.52) * mm, "mid": v(-121.9, -4.27) * mm, "end": v(-122.07, -4.09) * mm});
            skArc(sketch, "E359", {"start": v(-121.4, -3.4) * mm, "mid": v(-122.18, -3.3) * mm, "end": v(-122.07, -4.09) * mm});
            skArc(sketch, "E360", {"start": v(-121.4, -3.4) * mm, "mid": v(-121.2, -3.59) * mm, "end": v(-120.96, -3.65) * mm});
            skArc(sketch, "E361", {"start": v(-121.82, -103.32) * mm, "mid": v(-121.9, -103.07) * mm, "end": v(-122.07, -102.89) * mm});
            skArc(sketch, "E362", {"start": v(-121.4, -102.2) * mm, "mid": v(-122.18, -102.1) * mm, "end": v(-122.07, -102.89) * mm});
            skArc(sketch, "E363", {"start": v(-121.4, -102.2) * mm, "mid": v(-121.2, -102.39) * mm, "end": v(-120.96, -102.45) * mm});
            skLineSegment(sketch, "E364", {"start": v(-119.4, -102.45) * mm, "end": v(-120.96, -102.45) * mm});
            skArc(sketch, "E365", {"start": v(-119.4, -102.45) * mm, "mid": v(-119.14, -102.39) * mm, "end": v(-118.96, -102.2) * mm});
            skArc(sketch, "E366", {"start": v(-118.28, -102.89) * mm, "mid": v(-118.17, -102.1) * mm, "end": v(-118.96, -102.2) * mm});
            skArc(sketch, "E367", {"start": v(-118.28, -102.89) * mm, "mid": v(-118.46, -103.07) * mm, "end": v(-118.53, -103.32) * mm});
            skLineSegment(sketch, "E368", {"start": v(-118.52, -107.79) * mm, "end": v(-118.53, -103.32) * mm});
            skArc(sketch, "E369", {"start": v(-118.52, -107.79) * mm, "mid": v(-118.46, -108.04) * mm, "end": v(-118.27, -108.22) * mm});
            skArc(sketch, "E370", {"start": v(-118.96, -108.9) * mm, "mid": v(-118.17, -109) * mm, "end": v(-118.27, -108.22) * mm});
            skArc(sketch, "E371", {"start": v(-118.96, -108.9) * mm, "mid": v(-119.14, -108.72) * mm, "end": v(-119.4, -108.65) * mm});
            skLineSegment(sketch, "E372", {"start": v(-120.96, -108.65) * mm, "end": v(-119.4, -108.65) * mm});
            skArc(sketch, "E373", {"start": v(-120.96, -108.65) * mm, "mid": v(-121.2, -108.72) * mm, "end": v(-121.4, -108.9) * mm});
            skArc(sketch, "E374", {"start": v(-122.07, -108.22) * mm, "mid": v(-122.18, -109) * mm, "end": v(-121.4, -108.9) * mm});
            skArc(sketch, "E375", {"start": v(-122.07, -108.22) * mm, "mid": v(-121.9, -108.04) * mm, "end": v(-121.82, -107.79) * mm});
            skLineSegment(sketch, "E376", {"start": v(-121.82, -103.32) * mm, "end": v(-121.82, -107.79) * mm});
            skArc(sketch, "E377", {"start": v(-121.82, -124.52) * mm, "mid": v(-121.9, -124.27) * mm, "end": v(-122.07, -124.09) * mm});
            skArc(sketch, "E378", {"start": v(-121.4, -123.4) * mm, "mid": v(-122.18, -123.3) * mm, "end": v(-122.07, -124.09) * mm});
            skArc(sketch, "E379", {"start": v(-121.4, -123.4) * mm, "mid": v(-121.2, -123.59) * mm, "end": v(-120.96, -123.65) * mm});
            skLineSegment(sketch, "E380", {"start": v(-119.4, -123.65) * mm, "end": v(-120.96, -123.65) * mm});
            skArc(sketch, "E381", {"start": v(-119.4, -123.65) * mm, "mid": v(-119.14, -123.59) * mm, "end": v(-118.96, -123.4) * mm});
            skArc(sketch, "E382", {"start": v(-118.28, -124.09) * mm, "mid": v(-118.17, -123.3) * mm, "end": v(-118.96, -123.4) * mm});
            skArc(sketch, "E383", {"start": v(-118.28, -124.09) * mm, "mid": v(-118.46, -124.27) * mm, "end": v(-118.52, -124.52) * mm});
            skLineSegment(sketch, "E384", {"start": v(-118.52, -128.99) * mm, "end": v(-118.53, -124.52) * mm});
            skArc(sketch, "E385", {"start": v(-118.52, -128.99) * mm, "mid": v(-118.46, -129.24) * mm, "end": v(-118.27, -129.42) * mm});
            skArc(sketch, "E386", {"start": v(-118.96, -130.1) * mm, "mid": v(-118.17, -130.2) * mm, "end": v(-118.27, -129.42) * mm});
            skArc(sketch, "E387", {"start": v(-118.96, -130.1) * mm, "mid": v(-119.14, -129.92) * mm, "end": v(-119.4, -129.85) * mm});
            skLineSegment(sketch, "E388", {"start": v(-120.96, -129.85) * mm, "end": v(-119.4, -129.85) * mm});
            skArc(sketch, "E389", {"start": v(-120.96, -129.85) * mm, "mid": v(-121.2, -129.92) * mm, "end": v(-121.4, -130.1) * mm});
            skArc(sketch, "E390", {"start": v(-122.07, -129.42) * mm, "mid": v(-122.18, -130.2) * mm, "end": v(-121.4, -130.1) * mm});
            skArc(sketch, "E391", {"start": v(-122.07, -129.42) * mm, "mid": v(-121.9, -129.24) * mm, "end": v(-121.82, -128.99) * mm});
            skLineSegment(sketch, "E392", {"start": v(-121.82, -124.52) * mm, "end": v(-121.82, -128.99) * mm});
            skLineSegment(sketch, "E393", {"start": v(-140, -142.45) * mm, "end": v(-141.56, -142.45) * mm});
            skArc(sketch, "E394", {"start": v(-140, -142.45) * mm, "mid": v(-139.75, -142.39) * mm, "end": v(-139.56, -142.2) * mm});
            skArc(sketch, "E395", {"start": v(-138.88, -142.89) * mm, "mid": v(-138.78, -142.1) * mm, "end": v(-139.56, -142.2) * mm});
            skArc(sketch, "E396", {"start": v(-138.88, -142.89) * mm, "mid": v(-139.06, -143.07) * mm, "end": v(-139.13, -143.32) * mm});
            skLineSegment(sketch, "E397", {"start": v(-139.13, -147.79) * mm, "end": v(-139.13, -143.32) * mm});
            skArc(sketch, "E398", {"start": v(-139.13, -147.79) * mm, "mid": v(-139.06, -148.04) * mm, "end": v(-138.88, -148.22) * mm});
            skArc(sketch, "E399", {"start": v(-139.56, -148.9) * mm, "mid": v(-138.78, -149) * mm, "end": v(-138.88, -148.22) * mm});
            skArc(sketch, "E400", {"start": v(-139.56, -148.9) * mm, "mid": v(-139.75, -148.72) * mm, "end": v(-140, -148.65) * mm});
            skLineSegment(sketch, "E401", {"start": v(-141.56, -148.65) * mm, "end": v(-140, -148.65) * mm});
            skArc(sketch, "E402", {"start": v(-141.56, -148.65) * mm, "mid": v(-141.81, -148.72) * mm, "end": v(-142, -148.9) * mm});
            skArc(sketch, "E403", {"start": v(-142.68, -148.22) * mm, "mid": v(-142.78, -149) * mm, "end": v(-142, -148.9) * mm});
            skArc(sketch, "E404", {"start": v(-142.68, -148.22) * mm, "mid": v(-142.5, -148.04) * mm, "end": v(-142.43, -147.79) * mm});
            skLineSegment(sketch, "E405", {"start": v(-142.43, -143.32) * mm, "end": v(-142.43, -147.79) * mm});
            skArc(sketch, "E406", {"start": v(-142.43, -143.32) * mm, "mid": v(-142.5, -143.07) * mm, "end": v(-142.68, -142.89) * mm});
            skArc(sketch, "E407", {"start": v(-142, -142.2) * mm, "mid": v(-142.78, -142.1) * mm, "end": v(-142.68, -142.89) * mm});
            skArc(sketch, "E408", {"start": v(-142, -142.2) * mm, "mid": v(-141.81, -142.39) * mm, "end": v(-141.56, -142.45) * mm});
            skLineSegment(sketch, "E409", {"start": v(-140, -163.65) * mm, "end": v(-141.56, -163.65) * mm});
            skArc(sketch, "E410", {"start": v(-140, -163.65) * mm, "mid": v(-139.75, -163.59) * mm, "end": v(-139.56, -163.4) * mm});
            skArc(sketch, "E411", {"start": v(-138.88, -164.09) * mm, "mid": v(-138.78, -163.3) * mm, "end": v(-139.56, -163.4) * mm});
            skArc(sketch, "E412", {"start": v(-138.88, -164.09) * mm, "mid": v(-139.06, -164.27) * mm, "end": v(-139.13, -164.52) * mm});
            skLineSegment(sketch, "E413", {"start": v(-139.13, -168.99) * mm, "end": v(-139.13, -164.52) * mm});
            skArc(sketch, "E414", {"start": v(-139.13, -168.99) * mm, "mid": v(-139.06, -169.24) * mm, "end": v(-138.88, -169.42) * mm});
            skArc(sketch, "E415", {"start": v(-139.56, -170.1) * mm, "mid": v(-138.78, -170.2) * mm, "end": v(-138.88, -169.42) * mm});
            skArc(sketch, "E416", {"start": v(-139.56, -170.1) * mm, "mid": v(-139.75, -169.92) * mm, "end": v(-140, -169.85) * mm});
            skLineSegment(sketch, "E417", {"start": v(-141.56, -169.85) * mm, "end": v(-140, -169.85) * mm});
            skArc(sketch, "E418", {"start": v(-141.56, -169.85) * mm, "mid": v(-141.81, -169.92) * mm, "end": v(-142, -170.1) * mm});
            skArc(sketch, "E419", {"start": v(-142.68, -169.42) * mm, "mid": v(-142.78, -170.2) * mm, "end": v(-142, -170.1) * mm});
            skArc(sketch, "E420", {"start": v(-142.68, -169.42) * mm, "mid": v(-142.5, -169.24) * mm, "end": v(-142.43, -168.99) * mm});
            skLineSegment(sketch, "E421", {"start": v(-142.43, -164.52) * mm, "end": v(-142.43, -168.99) * mm});
            skArc(sketch, "E422", {"start": v(-142.43, -164.52) * mm, "mid": v(-142.5, -164.27) * mm, "end": v(-142.68, -164.09) * mm});
            skArc(sketch, "E423", {"start": v(-142, -163.4) * mm, "mid": v(-142.78, -163.3) * mm, "end": v(-142.68, -164.09) * mm});
            skArc(sketch, "E424", {"start": v(-142, -163.4) * mm, "mid": v(-141.81, -163.59) * mm, "end": v(-141.56, -163.65) * mm});
            skLineSegment(sketch, "E425", {"start": v(-157.8, -128.72) * mm, "end": v(-157.8, -130.3) * mm});
            skArc(sketch, "E426", {"start": v(-157.8, -128.72) * mm, "mid": v(-157.87, -128.47) * mm, "end": v(-158.05, -128.3) * mm});
            skArc(sketch, "E427", {"start": v(-157.37, -127.6) * mm, "mid": v(-158.15, -127.5) * mm, "end": v(-158.05, -128.3) * mm});
            skArc(sketch, "E428", {"start": v(-157.37, -127.6) * mm, "mid": v(-157.18, -127.8) * mm, "end": v(-156.93, -127.86) * mm});
            skLineSegment(sketch, "E429", {"start": v(-152.47, -127.86) * mm, "end": v(-156.93, -127.86) * mm});
            skArc(sketch, "E430", {"start": v(-152.47, -127.86) * mm, "mid": v(-152.22, -127.8) * mm, "end": v(-152.03, -127.6) * mm});
            skArc(sketch, "E431", {"start": v(-151.35, -128.3) * mm, "mid": v(-151.25, -127.5) * mm, "end": v(-152.03, -127.6) * mm});
            skArc(sketch, "E432", {"start": v(-151.35, -128.3) * mm, "mid": v(-151.53, -128.47) * mm, "end": v(-151.6, -128.72) * mm});
            skLineSegment(sketch, "E433", {"start": v(-151.6, -130.3) * mm, "end": v(-151.6, -128.72) * mm});
            skArc(sketch, "E434", {"start": v(-151.6, -130.3) * mm, "mid": v(-151.53, -130.54) * mm, "end": v(-151.35, -130.72) * mm});
            skArc(sketch, "E435", {"start": v(-152.03, -131.4) * mm, "mid": v(-151.25, -131.51) * mm, "end": v(-151.35, -130.72) * mm});
            skArc(sketch, "E436", {"start": v(-152.03, -131.4) * mm, "mid": v(-152.22, -131.22) * mm, "end": v(-152.47, -131.16) * mm});
            skLineSegment(sketch, "E437", {"start": v(-156.93, -131.16) * mm, "end": v(-152.47, -131.16) * mm});
            skArc(sketch, "E438", {"start": v(-156.93, -131.16) * mm, "mid": v(-157.18, -131.22) * mm, "end": v(-157.37, -131.4) * mm});
            skArc(sketch, "E439", {"start": v(-158.05, -130.72) * mm, "mid": v(-158.15, -131.51) * mm, "end": v(-157.37, -131.4) * mm});
            skArc(sketch, "E440", {"start": v(-158.05, -130.72) * mm, "mid": v(-157.87, -130.54) * mm, "end": v(-157.8, -130.3) * mm});
            skLineSegment(sketch, "E441", {"start": v(-179, -128.72) * mm, "end": v(-179, -130.3) * mm});
            skArc(sketch, "E442", {"start": v(-179, -128.72) * mm, "mid": v(-179.07, -128.47) * mm, "end": v(-179.25, -128.3) * mm});
            skArc(sketch, "E443", {"start": v(-178.57, -127.6) * mm, "mid": v(-179.35, -127.5) * mm, "end": v(-179.25, -128.3) * mm});
            skArc(sketch, "E444", {"start": v(-178.57, -127.6) * mm, "mid": v(-178.38, -127.8) * mm, "end": v(-178.13, -127.86) * mm});
            skLineSegment(sketch, "E445", {"start": v(-173.67, -127.86) * mm, "end": v(-178.13, -127.86) * mm});
            skArc(sketch, "E446", {"start": v(-173.67, -127.86) * mm, "mid": v(-173.42, -127.8) * mm, "end": v(-173.23, -127.6) * mm});
            skArc(sketch, "E447", {"start": v(-172.55, -128.3) * mm, "mid": v(-172.45, -127.5) * mm, "end": v(-173.23, -127.6) * mm});
            skArc(sketch, "E448", {"start": v(-172.55, -128.3) * mm, "mid": v(-172.73, -128.47) * mm, "end": v(-172.8, -128.72) * mm});
            skLineSegment(sketch, "E449", {"start": v(-172.8, -130.3) * mm, "end": v(-172.8, -128.72) * mm});
            skArc(sketch, "E450", {"start": v(-172.8, -130.3) * mm, "mid": v(-172.73, -130.54) * mm, "end": v(-172.55, -130.72) * mm});
            skArc(sketch, "E451", {"start": v(-173.23, -131.4) * mm, "mid": v(-172.45, -131.51) * mm, "end": v(-172.55, -130.72) * mm});
            skArc(sketch, "E452", {"start": v(-173.23, -131.4) * mm, "mid": v(-173.42, -131.22) * mm, "end": v(-173.67, -131.16) * mm});
            skLineSegment(sketch, "E453", {"start": v(-178.13, -131.16) * mm, "end": v(-173.67, -131.16) * mm});
            skArc(sketch, "E454", {"start": v(-178.13, -131.16) * mm, "mid": v(-178.38, -131.22) * mm, "end": v(-178.57, -131.4) * mm});
            skArc(sketch, "E455", {"start": v(-179.25, -130.72) * mm, "mid": v(-179.35, -131.51) * mm, "end": v(-178.57, -131.4) * mm});
            skArc(sketch, "E456", {"start": v(-179.25, -130.72) * mm, "mid": v(-179.07, -130.54) * mm, "end": v(-179, -130.3) * mm});
            skLineSegment(sketch, "E457", {"start": v(-189.04, -142.45) * mm, "end": v(-190.6, -142.45) * mm});
            skArc(sketch, "E458", {"start": v(-189.04, -142.45) * mm, "mid": v(-188.79, -142.39) * mm, "end": v(-188.6, -142.2) * mm});
            skArc(sketch, "E459", {"start": v(-187.92, -142.89) * mm, "mid": v(-187.82, -142.1) * mm, "end": v(-188.6, -142.2) * mm});
            skArc(sketch, "E460", {"start": v(-187.92, -142.89) * mm, "mid": v(-188.1, -143.07) * mm, "end": v(-188.17, -143.32) * mm});
            skLineSegment(sketch, "E461", {"start": v(-188.17, -147.79) * mm, "end": v(-188.17, -143.32) * mm});
            skArc(sketch, "E462", {"start": v(-188.17, -147.79) * mm, "mid": v(-188.1, -148.04) * mm, "end": v(-187.92, -148.22) * mm});
            skArc(sketch, "E463", {"start": v(-188.6, -148.9) * mm, "mid": v(-187.82, -149) * mm, "end": v(-187.92, -148.22) * mm});
            skArc(sketch, "E464", {"start": v(-188.6, -148.9) * mm, "mid": v(-188.79, -148.72) * mm, "end": v(-189.04, -148.65) * mm});
            skLineSegment(sketch, "E465", {"start": v(-190.6, -148.65) * mm, "end": v(-189.04, -148.65) * mm});
            skArc(sketch, "E466", {"start": v(-190.6, -148.65) * mm, "mid": v(-190.85, -148.72) * mm, "end": v(-191.04, -148.9) * mm});
            skArc(sketch, "E467", {"start": v(-191.72, -148.22) * mm, "mid": v(-191.82, -149) * mm, "end": v(-191.04, -148.9) * mm});
            skArc(sketch, "E468", {"start": v(-191.72, -148.22) * mm, "mid": v(-191.54, -148.04) * mm, "end": v(-191.47, -147.79) * mm});
            skLineSegment(sketch, "E469", {"start": v(-191.47, -143.32) * mm, "end": v(-191.47, -147.79) * mm});
            skArc(sketch, "E470", {"start": v(-191.47, -143.32) * mm, "mid": v(-191.54, -143.07) * mm, "end": v(-191.72, -142.89) * mm});
            skArc(sketch, "E471", {"start": v(-191.04, -142.2) * mm, "mid": v(-191.82, -142.1) * mm, "end": v(-191.72, -142.89) * mm});
            skArc(sketch, "E472", {"start": v(-191.04, -142.2) * mm, "mid": v(-190.85, -142.39) * mm, "end": v(-190.6, -142.45) * mm});
            skLineSegment(sketch, "E473", {"start": v(-189.04, -163.65) * mm, "end": v(-190.6, -163.65) * mm});
            skArc(sketch, "E474", {"start": v(-189.04, -163.65) * mm, "mid": v(-188.79, -163.59) * mm, "end": v(-188.6, -163.4) * mm});
            skArc(sketch, "E475", {"start": v(-187.92, -164.09) * mm, "mid": v(-187.82, -163.3) * mm, "end": v(-188.6, -163.4) * mm});
            skArc(sketch, "E476", {"start": v(-187.92, -164.09) * mm, "mid": v(-188.1, -164.27) * mm, "end": v(-188.17, -164.52) * mm});
            skLineSegment(sketch, "E477", {"start": v(-188.17, -168.99) * mm, "end": v(-188.17, -164.52) * mm});
            skArc(sketch, "E478", {"start": v(-188.17, -168.99) * mm, "mid": v(-188.1, -169.24) * mm, "end": v(-187.92, -169.42) * mm});
            skArc(sketch, "E479", {"start": v(-188.6, -170.1) * mm, "mid": v(-187.82, -170.2) * mm, "end": v(-187.92, -169.42) * mm});
            skArc(sketch, "E480", {"start": v(-188.6, -170.1) * mm, "mid": v(-188.79, -169.92) * mm, "end": v(-189.04, -169.85) * mm});
            skLineSegment(sketch, "E481", {"start": v(-190.6, -169.85) * mm, "end": v(-189.04, -169.85) * mm});
            skArc(sketch, "E482", {"start": v(-190.6, -169.85) * mm, "mid": v(-190.85, -169.92) * mm, "end": v(-191.04, -170.1) * mm});
            skArc(sketch, "E483", {"start": v(-191.72, -169.42) * mm, "mid": v(-191.82, -170.2) * mm, "end": v(-191.04, -170.1) * mm});
            skArc(sketch, "E484", {"start": v(-191.72, -169.42) * mm, "mid": v(-191.54, -169.24) * mm, "end": v(-191.47, -168.99) * mm});
            skLineSegment(sketch, "E485", {"start": v(-191.47, -164.52) * mm, "end": v(-191.47, -168.99) * mm});
            skArc(sketch, "E486", {"start": v(-191.47, -164.52) * mm, "mid": v(-191.54, -164.27) * mm, "end": v(-191.72, -164.09) * mm});
            skArc(sketch, "E487", {"start": v(-191.04, -163.4) * mm, "mid": v(-191.82, -163.3) * mm, "end": v(-191.72, -164.09) * mm});
            skArc(sketch, "E488", {"start": v(-191.04, -163.4) * mm, "mid": v(-190.85, -163.59) * mm, "end": v(-190.6, -163.65) * mm});
            skLineSegment(sketch, "E489", {"start": v(120.96, -142.45) * mm, "end": v(119.4, -142.45) * mm});
            skArc(sketch, "E490", {"start": v(120.96, -142.45) * mm, "mid": v(121.2, -142.39) * mm, "end": v(121.4, -142.2) * mm});
            skArc(sketch, "E491", {"start": v(122.07, -142.89) * mm, "mid": v(122.18, -142.1) * mm, "end": v(121.4, -142.2) * mm});
            skArc(sketch, "E492", {"start": v(122.07, -142.89) * mm, "mid": v(121.9, -143.07) * mm, "end": v(121.82, -143.32) * mm});
            skLineSegment(sketch, "E493", {"start": v(121.82, -168.99) * mm, "end": v(121.82, -143.32) * mm});
            skArc(sketch, "E494", {"start": v(121.82, -168.99) * mm, "mid": v(121.9, -169.24) * mm, "end": v(122.07, -169.42) * mm});
            skArc(sketch, "E495", {"start": v(121.4, -170.1) * mm, "mid": v(122.18, -170.2) * mm, "end": v(122.07, -169.42) * mm});
            skArc(sketch, "E496", {"start": v(121.4, -170.1) * mm, "mid": v(121.2, -169.92) * mm, "end": v(120.96, -169.85) * mm});
            skLineSegment(sketch, "E497", {"start": v(119.4, -169.85) * mm, "end": v(120.96, -169.85) * mm});
            skArc(sketch, "E498", {"start": v(119.4, -169.85) * mm, "mid": v(119.14, -169.92) * mm, "end": v(118.96, -170.1) * mm});
            skArc(sketch, "E499", {"start": v(118.28, -169.42) * mm, "mid": v(118.17, -170.2) * mm, "end": v(118.96, -170.1) * mm});
            skArc(sketch, "E500", {"start": v(118.28, -169.42) * mm, "mid": v(118.46, -169.24) * mm, "end": v(118.53, -168.99) * mm});
            skLineSegment(sketch, "E501", {"start": v(118.53, -143.32) * mm, "end": v(118.53, -168.99) * mm});
            skArc(sketch, "E502", {"start": v(118.53, -143.32) * mm, "mid": v(118.46, -143.07) * mm, "end": v(118.28, -142.89) * mm});
            skArc(sketch, "E503", {"start": v(118.96, -142.2) * mm, "mid": v(118.17, -142.1) * mm, "end": v(118.28, -142.89) * mm});
            skArc(sketch, "E504", {"start": v(118.96, -142.2) * mm, "mid": v(119.14, -142.39) * mm, "end": v(119.4, -142.45) * mm});
            skLineSegment(sketch, "E505", {"start": v(-119.4, -142.45) * mm, "end": v(-120.96, -142.45) * mm});
            skArc(sketch, "E506", {"start": v(-119.4, -142.45) * mm, "mid": v(-119.14, -142.39) * mm, "end": v(-118.96, -142.2) * mm});
            skArc(sketch, "E507", {"start": v(-118.28, -142.89) * mm, "mid": v(-118.17, -142.1) * mm, "end": v(-118.96, -142.2) * mm});
            skArc(sketch, "E508", {"start": v(-118.28, -142.89) * mm, "mid": v(-118.46, -143.07) * mm, "end": v(-118.53, -143.32) * mm});
            skLineSegment(sketch, "E509", {"start": v(-118.53, -168.99) * mm, "end": v(-118.53, -143.32) * mm});
            skArc(sketch, "E510", {"start": v(-118.53, -168.99) * mm, "mid": v(-118.46, -169.24) * mm, "end": v(-118.28, -169.42) * mm});
            skArc(sketch, "E511", {"start": v(-118.96, -170.1) * mm, "mid": v(-118.17, -170.2) * mm, "end": v(-118.28, -169.42) * mm});
            skArc(sketch, "E512", {"start": v(-118.96, -170.1) * mm, "mid": v(-119.14, -169.92) * mm, "end": v(-119.4, -169.85) * mm});
            skLineSegment(sketch, "E513", {"start": v(-120.96, -169.85) * mm, "end": v(-119.4, -169.85) * mm});
            skArc(sketch, "E514", {"start": v(-120.96, -169.85) * mm, "mid": v(-121.2, -169.92) * mm, "end": v(-121.4, -170.1) * mm});
            skArc(sketch, "E515", {"start": v(-122.07, -169.42) * mm, "mid": v(-122.18, -170.2) * mm, "end": v(-121.4, -170.1) * mm});
            skArc(sketch, "E516", {"start": v(-122.07, -169.42) * mm, "mid": v(-121.9, -169.24) * mm, "end": v(-121.82, -168.99) * mm});
            skLineSegment(sketch, "E517", {"start": v(-121.82, -143.32) * mm, "end": v(-121.82, -168.99) * mm});
            skArc(sketch, "E518", {"start": v(-121.82, -143.32) * mm, "mid": v(-121.9, -143.07) * mm, "end": v(-122.07, -142.89) * mm});
            skArc(sketch, "E519", {"start": v(-121.4, -142.2) * mm, "mid": v(-122.18, -142.1) * mm, "end": v(-122.07, -142.89) * mm});
            skArc(sketch, "E520", {"start": v(-121.4, -142.2) * mm, "mid": v(-121.2, -142.39) * mm, "end": v(-120.96, -142.45) * mm});
            skLineSegment(sketch, "E521", {"start": v(107, 138.85) * mm, "end": v(-107, 138.85) * mm});
            skArc(sketch, "E522", {"start": v(115, 130.85) * mm, "mid": v(112.66, 136.5) * mm, "end": v(107, 138.85) * mm});
            skLineSegment(sketch, "E523", {"start": v(115, -136.05) * mm, "end": v(115, 130.85) * mm});
            skArc(sketch, "E524", {"start": v(107, -144.03) * mm, "mid": v(112.65, -141.7) * mm, "end": v(115, -136.05) * mm});
            skLineSegment(sketch, "E525", {"start": v(30.55, -144.03) * mm, "end": v(107, -144.03) * mm});
            skArc(sketch, "E526", {"start": v(30.55, -144.03) * mm, "mid": v(27.95, -144.76) * mm, "end": v(26.1, -146.73) * mm});
            skLineSegment(sketch, "E527", {"start": v(17.44, -163.45) * mm, "end": v(26.1, -146.73) * mm});
            skArc(sketch, "E528", {"start": v(13, -166.15) * mm, "mid": v(15.6, -165.42) * mm, "end": v(17.44, -163.45) * mm});
            skLineSegment(sketch, "E529", {"start": v(-13, -166.15) * mm, "end": v(13, -166.15) * mm});
            skArc(sketch, "E530", {"start": v(-17.45, -163.44) * mm, "mid": v(-15.6, -165.42) * mm, "end": v(-13, -166.15) * mm});
            skLineSegment(sketch, "E531", {"start": v(-26.03, -146.74) * mm, "end": v(-17.45, -163.44) * mm});
            skArc(sketch, "E532", {"start": v(-26.03, -146.74) * mm, "mid": v(-27.87, -144.76) * mm, "end": v(-30.48, -144.03) * mm});
            skLineSegment(sketch, "E533", {"start": v(-107, -144.03) * mm, "end": v(-30.48, -144.03) * mm});
            skArc(sketch, "E534", {"start": v(-115, -136.05) * mm, "mid": v(-112.65, -141.7) * mm, "end": v(-107, -144.03) * mm});
            skLineSegment(sketch, "E535", {"start": v(-115, 130.85) * mm, "end": v(-115, -136.05) * mm});
            skArc(sketch, "E536", {"start": v(-107, 138.85) * mm, "mid": v(-112.66, 136.5) * mm, "end": v(-115, 130.85) * mm});
            skArc(sketch, "E537", {"start": v(190, -181.15) * mm, "mid": v(193.54, -179.69) * mm, "end": v(195, -176.15) * mm});
            skLineSegment(sketch, "E538", {"start": v(195, -176.15) * mm, "end": v(195, -127.62) * mm});
            skArc(sketch, "E539", {"start": v(195, -127.62) * mm, "mid": v(194.55, -125.34) * mm, "end": v(193.27, -123.4) * mm});
            skLineSegment(sketch, "E540", {"start": v(193.27, -123.4) * mm, "end": v(188.73, -118.8) * mm});
            skArc(sketch, "E541", {"start": v(187, -114.6) * mm, "mid": v(187.45, -116.87) * mm, "end": v(188.73, -118.8) * mm});
            skLineSegment(sketch, "E542", {"start": v(187, -114.6) * mm, "end": v(187, 166.36) * mm});
            skArc(sketch, "E543", {"start": v(188.76, 170.6) * mm, "mid": v(187.46, 168.66) * mm, "end": v(187, 166.36) * mm});
            skLineSegment(sketch, "E544", {"start": v(188.76, 170.6) * mm, "end": v(193.24, 175.09) * mm});
            skArc(sketch, "E545", {"start": v(193.24, 175.09) * mm, "mid": v(194.54, 177.04) * mm, "end": v(195, 179.33) * mm});
            skLineSegment(sketch, "E546", {"start": v(195, 179.33) * mm, "end": v(195, 188.85) * mm});
            skLineSegment(sketch, "E547", {"start": v(195, 188.85) * mm, "end": v(185, 188.85) * mm});
            skLineSegment(sketch, "E548", {"start": v(185, 188.85) * mm, "end": v(185, 186.61) * mm});
            skArc(sketch, "E549", {"start": v(185, 186.61) * mm, "mid": v(185.07, 186.36) * mm, "end": v(185.25, 186.18) * mm});
            skArc(sketch, "E550", {"start": v(184.57, 185.5) * mm, "mid": v(185.35, 185.4) * mm, "end": v(185.25, 186.18) * mm});
            skArc(sketch, "E551", {"start": v(184.57, 185.5) * mm, "mid": v(184.38, 185.68) * mm, "end": v(184.13, 185.75) * mm});
            skLineSegment(sketch, "E552", {"start": v(184.13, 185.75) * mm, "end": v(160.78, 185.75) * mm});
            skLineSegment(sketch, "E553", {"start": v(160.78, 185.75) * mm, "end": v(160.78, 182.75) * mm});
            skLineSegment(sketch, "E554", {"start": v(160.78, 182.75) * mm, "end": v(162.05, 182.75) * mm});
            skLineSegment(sketch, "E555", {"start": v(162.05, 182.75) * mm, "end": v(162.05, 178.75) * mm});
            skLineSegment(sketch, "E556", {"start": v(162.05, 178.75) * mm, "end": v(160.78, 178.75) * mm});
            skLineSegment(sketch, "E557", {"start": v(160.78, 178.75) * mm, "end": v(160.78, 175.75) * mm});
            skLineSegment(sketch, "E558", {"start": v(160.78, 175.75) * mm, "end": v(157.57, 175.75) * mm});
            skLineSegment(sketch, "E559", {"start": v(157.57, 175.75) * mm, "end": v(157.57, 178.75) * mm});
            skLineSegment(sketch, "E560", {"start": v(157.57, 178.75) * mm, "end": v(156.3, 178.75) * mm});
            skLineSegment(sketch, "E561", {"start": v(156.3, 178.75) * mm, "end": v(156.3, 182.75) * mm});
            skLineSegment(sketch, "E562", {"start": v(156.3, 182.75) * mm, "end": v(157.57, 182.75) * mm});
            skLineSegment(sketch, "E563", {"start": v(157.57, 182.75) * mm, "end": v(157.57, 185.75) * mm});
            skLineSegment(sketch, "E564", {"start": v(157.57, 185.75) * mm, "end": v(134.07, 185.75) * mm});
            skArc(sketch, "E565", {"start": v(134.07, 185.75) * mm, "mid": v(133.82, 185.68) * mm, "end": v(133.63, 185.5) * mm});
            skArc(sketch, "E566", {"start": v(132.95, 186.18) * mm, "mid": v(132.85, 185.4) * mm, "end": v(133.63, 185.5) * mm});
            skArc(sketch, "E567", {"start": v(132.95, 186.18) * mm, "mid": v(133.13, 186.36) * mm, "end": v(133.2, 186.61) * mm});
            skLineSegment(sketch, "E568", {"start": v(133.2, 186.61) * mm, "end": v(133.2, 188.85) * mm});
            skLineSegment(sketch, "E569", {"start": v(133.2, 188.85) * mm, "end": v(51.73, 188.85) * mm});
            skLineSegment(sketch, "E570", {"start": v(51.73, 188.85) * mm, "end": v(51.73, 186.61) * mm});
            skArc(sketch, "E571", {"start": v(51.73, 186.61) * mm, "mid": v(51.8, 186.36) * mm, "end": v(51.98, 186.18) * mm});
            skArc(sketch, "E572", {"start": v(51.3, 185.5) * mm, "mid": v(52.09, 185.4) * mm, "end": v(51.98, 186.18) * mm});
            skArc(sketch, "E573", {"start": v(51.3, 185.5) * mm, "mid": v(51.12, 185.68) * mm, "end": v(50.87, 185.75) * mm});
            skLineSegment(sketch, "E574", {"start": v(50.87, 185.75) * mm, "end": v(44.1, 185.75) * mm});
            skLineSegment(sketch, "E575", {"start": v(44.1, 185.75) * mm, "end": v(44.1, 182.75) * mm});
            skLineSegment(sketch, "E576", {"start": v(44.1, 182.75) * mm, "end": v(45.38, 182.75) * mm});
            skLineSegment(sketch, "E577", {"start": v(45.38, 182.75) * mm, "end": v(45.38, 178.75) * mm});
            skLineSegment(sketch, "E578", {"start": v(45.38, 178.75) * mm, "end": v(44.1, 178.75) * mm});
            skLineSegment(sketch, "E579", {"start": v(44.1, 178.75) * mm, "end": v(44.1, 175.75) * mm});
            skLineSegment(sketch, "E580", {"start": v(44.1, 175.75) * mm, "end": v(40.9, 175.75) * mm});
            skLineSegment(sketch, "E581", {"start": v(40.9, 175.75) * mm, "end": v(40.9, 178.75) * mm});
            skLineSegment(sketch, "E582", {"start": v(40.9, 178.75) * mm, "end": v(39.63, 178.75) * mm});
            skLineSegment(sketch, "E583", {"start": v(39.63, 178.75) * mm, "end": v(39.63, 182.75) * mm});
            skLineSegment(sketch, "E584", {"start": v(39.63, 182.75) * mm, "end": v(40.9, 182.75) * mm});
            skLineSegment(sketch, "E585", {"start": v(40.9, 182.75) * mm, "end": v(40.9, 185.75) * mm});
            skLineSegment(sketch, "E586", {"start": v(40.9, 185.75) * mm, "end": v(34.13, 185.75) * mm});
            skArc(sketch, "E587", {"start": v(34.13, 185.75) * mm, "mid": v(33.88, 185.68) * mm, "end": v(33.7, 185.5) * mm});
            skArc(sketch, "E588", {"start": v(33.02, 186.18) * mm, "mid": v(32.91, 185.4) * mm, "end": v(33.7, 185.5) * mm});
            skArc(sketch, "E589", {"start": v(33.02, 186.18) * mm, "mid": v(33.2, 186.36) * mm, "end": v(33.27, 186.61) * mm});
            skLineSegment(sketch, "E590", {"start": v(33.27, 186.61) * mm, "end": v(33.27, 188.85) * mm});
            skLineSegment(sketch, "E591", {"start": v(33.27, 188.85) * mm, "end": v(-33.27, 188.85) * mm});
            skLineSegment(sketch, "E592", {"start": v(-33.27, 188.85) * mm, "end": v(-33.27, 186.61) * mm});
            skArc(sketch, "E593", {"start": v(-33.27, 186.61) * mm, "mid": v(-33.2, 186.36) * mm, "end": v(-33.02, 186.18) * mm});
            skArc(sketch, "E594", {"start": v(-33.7, 185.5) * mm, "mid": v(-32.91, 185.4) * mm, "end": v(-33.02, 186.18) * mm});
            skArc(sketch, "E595", {"start": v(-33.7, 185.5) * mm, "mid": v(-33.88, 185.68) * mm, "end": v(-34.13, 185.75) * mm});
            skLineSegment(sketch, "E596", {"start": v(-34.13, 185.75) * mm, "end": v(-40.9, 185.75) * mm});
            skLineSegment(sketch, "E597", {"start": v(-40.9, 185.75) * mm, "end": v(-40.9, 182.75) * mm});
            skLineSegment(sketch, "E598", {"start": v(-40.9, 182.75) * mm, "end": v(-39.63, 182.75) * mm});
            skLineSegment(sketch, "E599", {"start": v(-39.63, 182.75) * mm, "end": v(-39.63, 178.75) * mm});
            skLineSegment(sketch, "E600", {"start": v(-39.63, 178.75) * mm, "end": v(-40.9, 178.75) * mm});
            skLineSegment(sketch, "E601", {"start": v(-40.9, 178.75) * mm, "end": v(-40.9, 175.75) * mm});
            skLineSegment(sketch, "E602", {"start": v(-40.9, 175.75) * mm, "end": v(-44.1, 175.75) * mm});
            skLineSegment(sketch, "E603", {"start": v(-44.1, 175.75) * mm, "end": v(-44.1, 178.75) * mm});
            skLineSegment(sketch, "E604", {"start": v(-44.1, 178.75) * mm, "end": v(-45.38, 178.75) * mm});
            skLineSegment(sketch, "E605", {"start": v(-45.38, 178.75) * mm, "end": v(-45.38, 182.75) * mm});
            skLineSegment(sketch, "E606", {"start": v(-45.38, 182.75) * mm, "end": v(-44.1, 182.75) * mm});
            skLineSegment(sketch, "E607", {"start": v(-44.1, 182.75) * mm, "end": v(-44.1, 185.75) * mm});
            skLineSegment(sketch, "E608", {"start": v(-44.1, 185.75) * mm, "end": v(-50.88, 185.75) * mm});
            skArc(sketch, "E609", {"start": v(-50.88, 185.75) * mm, "mid": v(-51.13, 185.68) * mm, "end": v(-51.3, 185.5) * mm});
            skArc(sketch, "E610", {"start": v(-52, 186.18) * mm, "mid": v(-52.1, 185.4) * mm, "end": v(-51.3, 185.5) * mm});
            skArc(sketch, "E611", {"start": v(-52, 186.18) * mm, "mid": v(-51.8, 186.36) * mm, "end": v(-51.74, 186.61) * mm});
            skLineSegment(sketch, "E612", {"start": v(-51.74, 186.61) * mm, "end": v(-51.74, 188.85) * mm});
            skLineSegment(sketch, "E613", {"start": v(-51.74, 188.85) * mm, "end": v(-133.2, 188.85) * mm});
            skLineSegment(sketch, "E614", {"start": v(-133.2, 188.85) * mm, "end": v(-133.2, 186.61) * mm});
            skArc(sketch, "E615", {"start": v(-133.2, 186.61) * mm, "mid": v(-133.13, 186.36) * mm, "end": v(-132.95, 186.18) * mm});
            skArc(sketch, "E616", {"start": v(-133.63, 185.5) * mm, "mid": v(-132.85, 185.4) * mm, "end": v(-132.95, 186.18) * mm});
            skArc(sketch, "E617", {"start": v(-133.63, 185.5) * mm, "mid": v(-133.82, 185.68) * mm, "end": v(-134.07, 185.75) * mm});
            skLineSegment(sketch, "E618", {"start": v(-134.07, 185.75) * mm, "end": v(-157.57, 185.75) * mm});
            skLineSegment(sketch, "E619", {"start": v(-157.57, 185.75) * mm, "end": v(-157.57, 182.75) * mm});
            skLineSegment(sketch, "E620", {"start": v(-157.57, 182.75) * mm, "end": v(-156.3, 182.75) * mm});
            skLineSegment(sketch, "E621", {"start": v(-156.3, 182.75) * mm, "end": v(-156.3, 178.75) * mm});
            skLineSegment(sketch, "E622", {"start": v(-156.3, 178.75) * mm, "end": v(-157.57, 178.75) * mm});
            skLineSegment(sketch, "E623", {"start": v(-157.57, 178.75) * mm, "end": v(-157.57, 175.75) * mm});
            skLineSegment(sketch, "E624", {"start": v(-157.57, 175.75) * mm, "end": v(-160.78, 175.75) * mm});
            skLineSegment(sketch, "E625", {"start": v(-160.78, 175.75) * mm, "end": v(-160.78, 178.75) * mm});
            skLineSegment(sketch, "E626", {"start": v(-160.78, 178.75) * mm, "end": v(-162.05, 178.75) * mm});
            skLineSegment(sketch, "E627", {"start": v(-162.05, 178.75) * mm, "end": v(-162.05, 182.75) * mm});
            skLineSegment(sketch, "E628", {"start": v(-162.05, 182.75) * mm, "end": v(-160.78, 182.75) * mm});
            skLineSegment(sketch, "E629", {"start": v(-160.78, 182.75) * mm, "end": v(-160.78, 185.75) * mm});
            skLineSegment(sketch, "E630", {"start": v(-160.78, 185.75) * mm, "end": v(-184.13, 185.75) * mm});
            skArc(sketch, "E631", {"start": v(-184.13, 185.75) * mm, "mid": v(-184.38, 185.68) * mm, "end": v(-184.57, 185.5) * mm});
            skArc(sketch, "E632", {"start": v(-185.25, 186.18) * mm, "mid": v(-185.35, 185.4) * mm, "end": v(-184.57, 185.5) * mm});
            skArc(sketch, "E633", {"start": v(-185.25, 186.18) * mm, "mid": v(-185.07, 186.36) * mm, "end": v(-185, 186.61) * mm});
            skLineSegment(sketch, "E634", {"start": v(-185, 186.61) * mm, "end": v(-185, 188.85) * mm});
            skLineSegment(sketch, "E635", {"start": v(-185, 188.85) * mm, "end": v(-195, 188.85) * mm});
            skLineSegment(sketch, "E636", {"start": v(-195, 188.85) * mm, "end": v(-195, 179.33) * mm});
            skArc(sketch, "E637", {"start": v(-195, 179.33) * mm, "mid": v(-194.54, 177.04) * mm, "end": v(-193.24, 175.09) * mm});
            skLineSegment(sketch, "E638", {"start": v(-193.24, 175.09) * mm, "end": v(-188.76, 170.6) * mm});
            skArc(sketch, "E639", {"start": v(-187, 166.36) * mm, "mid": v(-187.46, 168.66) * mm, "end": v(-188.76, 170.6) * mm});
            skLineSegment(sketch, "E640", {"start": v(-187, 166.36) * mm, "end": v(-187, -114.67) * mm});
            skArc(sketch, "E641", {"start": v(-188.76, -118.91) * mm, "mid": v(-187.46, -116.96) * mm, "end": v(-187, -114.67) * mm});
            skLineSegment(sketch, "E642", {"start": v(-188.76, -118.91) * mm, "end": v(-193.24, -123.4) * mm});
            skArc(sketch, "E643", {"start": v(-193.24, -123.4) * mm, "mid": v(-194.54, -125.34) * mm, "end": v(-195, -127.64) * mm});
            skLineSegment(sketch, "E644", {"start": v(-195, -127.64) * mm, "end": v(-195, -176.15) * mm});
            skArc(sketch, "E645", {"start": v(-195, -176.15) * mm, "mid": v(-193.54, -179.69) * mm, "end": v(-190, -181.15) * mm});
            skLineSegment(sketch, "E646", {"start": v(-190, -181.15) * mm, "end": v(-100.41, -181.15) * mm});
            skArc(sketch, "E647", {"start": v(-100.41, -181.15) * mm, "mid": v(-100.03, -181.08) * mm, "end": v(-99.7, -180.86) * mm});
            skLineSegment(sketch, "E648", {"start": v(-99.7, -180.86) * mm, "end": v(-98.3, -179.45) * mm});
            skArc(sketch, "E649", {"start": v(-97.59, -179.15) * mm, "mid": v(-97.97, -179.23) * mm, "end": v(-98.3, -179.45) * mm});
            skLineSegment(sketch, "E650", {"start": v(-97.59, -179.15) * mm, "end": v(97.59, -179.15) * mm});
            skArc(sketch, "E651", {"start": v(98.3, -179.45) * mm, "mid": v(97.97, -179.23) * mm, "end": v(97.59, -179.15) * mm});
            skLineSegment(sketch, "E652", {"start": v(98.3, -179.45) * mm, "end": v(99.7, -180.86) * mm});
            skArc(sketch, "E653", {"start": v(99.7, -180.86) * mm, "mid": v(100.03, -181.08) * mm, "end": v(100.41, -181.15) * mm});
            skLineSegment(sketch, "E654", {"start": v(100.41, -181.15) * mm, "end": v(190, -181.15) * mm});
            skCircle(sketch, "E655", {"center": v(-189.82, -156.15) * mm, "radius": 1.6 * mm});
            skCircle(sketch, "E656", {"center": v(-140.78, -156.15) * mm, "radius": 1.6 * mm});
            skCircle(sketch, "E657", {"center": v(-120.18, 3.85) * mm, "radius": 1.6 * mm});
            skCircle(sketch, "E658", {"center": v(120.18, -116.15) * mm, "radius": 1.6 * mm});
            skCircle(sketch, "E659", {"center": v(120.17, 163.85) * mm, "radius": 1.6 * mm});
            skCircle(sketch, "E660", {"center": v(165.3, -129.5) * mm, "radius": 1.6 * mm});
            skCircle(sketch, "E661", {"center": v(-58.53, -156.15) * mm, "radius": 1.6 * mm});
            skLineSegment(sketch, "E662", {"start": v(44.83, -155.37) * mm, "end": v(44.83, -156.94) * mm});
            skArc(sketch, "E663", {"start": v(44.83, -155.37) * mm, "mid": v(44.76, -155.12) * mm, "end": v(44.58, -154.94) * mm});
            skArc(sketch, "E664", {"start": v(45.26, -154.25) * mm, "mid": v(44.47, -154.15) * mm, "end": v(44.58, -154.94) * mm});
            skArc(sketch, "E665", {"start": v(45.26, -154.25) * mm, "mid": v(45.44, -154.44) * mm, "end": v(45.7, -154.5) * mm});
            skLineSegment(sketch, "E666", {"start": v(50.16, -154.5) * mm, "end": v(45.7, -154.5) * mm});
            skArc(sketch, "E667", {"start": v(50.16, -154.5) * mm, "mid": v(50.4, -154.44) * mm, "end": v(50.6, -154.25) * mm});
            skArc(sketch, "E668", {"start": v(51.28, -154.94) * mm, "mid": v(51.38, -154.15) * mm, "end": v(50.6, -154.25) * mm});
            skArc(sketch, "E669", {"start": v(51.28, -154.94) * mm, "mid": v(51.1, -155.12) * mm, "end": v(51.03, -155.37) * mm});
            skLineSegment(sketch, "E670", {"start": v(51.03, -156.94) * mm, "end": v(51.03, -155.37) * mm});
            skArc(sketch, "E671", {"start": v(51.03, -156.94) * mm, "mid": v(51.1, -157.19) * mm, "end": v(51.28, -157.37) * mm});
            skArc(sketch, "E672", {"start": v(50.6, -158.05) * mm, "mid": v(51.38, -158.16) * mm, "end": v(51.28, -157.37) * mm});
            skArc(sketch, "E673", {"start": v(50.6, -158.05) * mm, "mid": v(50.4, -157.87) * mm, "end": v(50.16, -157.8) * mm});
            skLineSegment(sketch, "E674", {"start": v(45.7, -157.8) * mm, "end": v(50.16, -157.8) * mm});
            skArc(sketch, "E675", {"start": v(45.7, -157.8) * mm, "mid": v(45.44, -157.87) * mm, "end": v(45.26, -158.05) * mm});
            skArc(sketch, "E676", {"start": v(44.58, -157.37) * mm, "mid": v(44.47, -158.16) * mm, "end": v(45.26, -158.05) * mm});
            skArc(sketch, "E677", {"start": v(44.58, -157.37) * mm, "mid": v(44.76, -157.19) * mm, "end": v(44.83, -156.94) * mm});
            skLineSegment(sketch, "E678", {"start": v(66.03, -155.37) * mm, "end": v(66.03, -156.94) * mm});
            skArc(sketch, "E679", {"start": v(66.03, -155.37) * mm, "mid": v(65.96, -155.12) * mm, "end": v(65.78, -154.94) * mm});
            skArc(sketch, "E680", {"start": v(66.46, -154.25) * mm, "mid": v(65.67, -154.15) * mm, "end": v(65.78, -154.94) * mm});
            skArc(sketch, "E681", {"start": v(66.46, -154.25) * mm, "mid": v(66.64, -154.44) * mm, "end": v(66.9, -154.5) * mm});
            skLineSegment(sketch, "E682", {"start": v(71.36, -154.5) * mm, "end": v(66.9, -154.5) * mm});
            skArc(sketch, "E683", {"start": v(71.36, -154.5) * mm, "mid": v(71.6, -154.44) * mm, "end": v(71.8, -154.25) * mm});
            skArc(sketch, "E684", {"start": v(72.48, -154.94) * mm, "mid": v(72.58, -154.15) * mm, "end": v(71.8, -154.25) * mm});
            skArc(sketch, "E685", {"start": v(72.48, -154.94) * mm, "mid": v(72.3, -155.12) * mm, "end": v(72.23, -155.37) * mm});
            skLineSegment(sketch, "E686", {"start": v(72.23, -156.94) * mm, "end": v(72.23, -155.37) * mm});
            skArc(sketch, "E687", {"start": v(72.23, -156.94) * mm, "mid": v(72.3, -157.19) * mm, "end": v(72.48, -157.37) * mm});
            skArc(sketch, "E688", {"start": v(71.8, -158.05) * mm, "mid": v(72.58, -158.16) * mm, "end": v(72.48, -157.37) * mm});
            skArc(sketch, "E689", {"start": v(71.8, -158.05) * mm, "mid": v(71.6, -157.87) * mm, "end": v(71.36, -157.8) * mm});
            skLineSegment(sketch, "E690", {"start": v(66.9, -157.8) * mm, "end": v(71.36, -157.8) * mm});
            skArc(sketch, "E691", {"start": v(66.9, -157.8) * mm, "mid": v(66.64, -157.87) * mm, "end": v(66.46, -158.05) * mm});
            skArc(sketch, "E692", {"start": v(65.78, -157.37) * mm, "mid": v(65.67, -158.16) * mm, "end": v(66.46, -158.05) * mm});
            skArc(sketch, "E693", {"start": v(65.78, -157.37) * mm, "mid": v(65.96, -157.19) * mm, "end": v(66.03, -156.94) * mm});
            skCircle(sketch, "E694", {"center": v(79.02, -171.15) * mm, "radius": 1.6 * mm});
            skCircle(sketch, "E695", {"center": v(-39.5, -171.15) * mm, "radius": 1.6 * mm});
            skCircle(sketch, "E696", {"center": v(-165.3, -141.15) * mm, "radius": 1.6 * mm});
            skLineSegment(sketch, "E697", {"start": v(151.6, -140.37) * mm, "end": v(151.6, -141.94) * mm});
            skArc(sketch, "E698", {"start": v(151.6, -140.37) * mm, "mid": v(151.53, -140.12) * mm, "end": v(151.35, -139.94) * mm});
            skArc(sketch, "E699", {"start": v(152.03, -139.25) * mm, "mid": v(151.25, -139.15) * mm, "end": v(151.35, -139.94) * mm});
            skArc(sketch, "E700", {"start": v(152.03, -139.25) * mm, "mid": v(152.22, -139.44) * mm, "end": v(152.47, -139.5) * mm});
            skLineSegment(sketch, "E701", {"start": v(156.93, -139.5) * mm, "end": v(152.47, -139.5) * mm});
            skArc(sketch, "E702", {"start": v(156.93, -139.5) * mm, "mid": v(157.18, -139.44) * mm, "end": v(157.37, -139.25) * mm});
            skArc(sketch, "E703", {"start": v(158.05, -139.94) * mm, "mid": v(158.15, -139.15) * mm, "end": v(157.37, -139.25) * mm});
            skArc(sketch, "E704", {"start": v(158.05, -139.94) * mm, "mid": v(157.87, -140.12) * mm, "end": v(157.8, -140.37) * mm});
            skLineSegment(sketch, "E705", {"start": v(157.8, -141.94) * mm, "end": v(157.8, -140.37) * mm});
            skArc(sketch, "E706", {"start": v(157.8, -141.94) * mm, "mid": v(157.87, -142.19) * mm, "end": v(158.05, -142.37) * mm});
            skArc(sketch, "E707", {"start": v(157.37, -143.05) * mm, "mid": v(158.15, -143.16) * mm, "end": v(158.05, -142.37) * mm});
            skArc(sketch, "E708", {"start": v(157.37, -143.05) * mm, "mid": v(157.18, -142.87) * mm, "end": v(156.93, -142.8) * mm});
            skLineSegment(sketch, "E709", {"start": v(152.47, -142.8) * mm, "end": v(156.93, -142.8) * mm});
            skArc(sketch, "E710", {"start": v(152.47, -142.8) * mm, "mid": v(152.22, -142.87) * mm, "end": v(152.03, -143.05) * mm});
            skArc(sketch, "E711", {"start": v(151.35, -142.37) * mm, "mid": v(151.25, -143.16) * mm, "end": v(152.03, -143.05) * mm});
            skArc(sketch, "E712", {"start": v(151.35, -142.37) * mm, "mid": v(151.53, -142.19) * mm, "end": v(151.6, -141.94) * mm});
            skLineSegment(sketch, "E713", {"start": v(172.8, -140.37) * mm, "end": v(172.8, -141.94) * mm});
            skArc(sketch, "E714", {"start": v(172.8, -140.37) * mm, "mid": v(172.73, -140.12) * mm, "end": v(172.55, -139.94) * mm});
            skArc(sketch, "E715", {"start": v(173.23, -139.25) * mm, "mid": v(172.45, -139.15) * mm, "end": v(172.55, -139.94) * mm});
            skArc(sketch, "E716", {"start": v(173.23, -139.25) * mm, "mid": v(173.42, -139.44) * mm, "end": v(173.67, -139.5) * mm});
            skLineSegment(sketch, "E717", {"start": v(178.13, -139.5) * mm, "end": v(173.67, -139.5) * mm});
            skArc(sketch, "E718", {"start": v(178.13, -139.5) * mm, "mid": v(178.38, -139.44) * mm, "end": v(178.57, -139.25) * mm});
            skArc(sketch, "E719", {"start": v(179.25, -139.94) * mm, "mid": v(179.35, -139.15) * mm, "end": v(178.57, -139.25) * mm});
            skArc(sketch, "E720", {"start": v(179.25, -139.94) * mm, "mid": v(179.07, -140.12) * mm, "end": v(179, -140.37) * mm});
            skLineSegment(sketch, "E721", {"start": v(179, -141.94) * mm, "end": v(179, -140.37) * mm});
            skArc(sketch, "E722", {"start": v(179, -141.94) * mm, "mid": v(179.07, -142.19) * mm, "end": v(179.25, -142.37) * mm});
            skArc(sketch, "E723", {"start": v(178.57, -143.05) * mm, "mid": v(179.35, -143.16) * mm, "end": v(179.25, -142.37) * mm});
            skArc(sketch, "E724", {"start": v(178.57, -143.05) * mm, "mid": v(178.38, -142.87) * mm, "end": v(178.13, -142.8) * mm});
            skLineSegment(sketch, "E725", {"start": v(173.67, -142.8) * mm, "end": v(178.13, -142.8) * mm});
            skArc(sketch, "E726", {"start": v(173.67, -142.8) * mm, "mid": v(173.42, -142.87) * mm, "end": v(173.23, -143.05) * mm});
            skArc(sketch, "E727", {"start": v(172.55, -142.37) * mm, "mid": v(172.45, -143.16) * mm, "end": v(173.23, -143.05) * mm});
            skArc(sketch, "E728", {"start": v(172.55, -142.37) * mm, "mid": v(172.73, -142.19) * mm, "end": v(172.8, -141.94) * mm});
            skCircle(sketch, "E729", {"center": v(0, -171.15) * mm, "radius": 1.6 * mm});
            skLineSegment(sketch, "E730", {"start": v(136, -120.15) * mm, "end": v(136, -112.15) * mm});
            skArc(sketch, "E731", {"start": v(128, -120.15) * mm, "mid": v(132, -124.15) * mm, "end": v(136, -120.15) * mm});
            skLineSegment(sketch, "E732", {"start": v(128, -112.15) * mm, "end": v(128, -120.15) * mm});
            skArc(sketch, "E733", {"start": v(136, -112.15) * mm, "mid": v(132, -108.15) * mm, "end": v(128, -112.15) * mm});
            skLineSegment(sketch, "E734", {"start": v(172.2, -76.15) * mm, "end": v(172.2, -116.15) * mm});
            skArc(sketch, "E735", {"start": v(175.4, -76.15) * mm, "mid": v(173.8, -74.55) * mm, "end": v(172.2, -76.15) * mm});
            skLineSegment(sketch, "E736", {"start": v(175.4, -116.15) * mm, "end": v(175.4, -76.15) * mm});
            skArc(sketch, "E737", {"start": v(172.2, -116.15) * mm, "mid": v(173.8, -117.75) * mm, "end": v(175.4, -116.15) * mm});
            skLineSegment(sketch, "E738", {"start": v(153.2, -76.15) * mm, "end": v(153.2, -116.15) * mm});
            skArc(sketch, "E739", {"start": v(156.4, -76.15) * mm, "mid": v(154.8, -74.55) * mm, "end": v(153.2, -76.15) * mm});
            skLineSegment(sketch, "E740", {"start": v(156.4, -116.15) * mm, "end": v(156.4, -76.15) * mm});
            skArc(sketch, "E741", {"start": v(153.2, -116.15) * mm, "mid": v(154.8, -117.75) * mm, "end": v(156.4, -116.15) * mm});
            skLineSegment(sketch, "E742", {"start": v(162.7, -76.15) * mm, "end": v(162.7, -116.15) * mm});
            skArc(sketch, "E743", {"start": v(165.9, -76.15) * mm, "mid": v(164.3, -74.55) * mm, "end": v(162.7, -76.15) * mm});
            skLineSegment(sketch, "E744", {"start": v(165.9, -116.15) * mm, "end": v(165.9, -76.15) * mm});
            skArc(sketch, "E745", {"start": v(162.7, -116.15) * mm, "mid": v(164.3, -117.75) * mm, "end": v(165.9, -116.15) * mm});
            skLineSegment(sketch, "E746", {"start": v(174.5, 8.95) * mm, "end": v(169.5, 8.95) * mm});
            skArc(sketch, "E747", {"start": v(174.5, 5.75) * mm, "mid": v(176.1, 7.35) * mm, "end": v(174.5, 8.95) * mm});
            skLineSegment(sketch, "E748", {"start": v(169.5, 5.75) * mm, "end": v(174.5, 5.75) * mm});
            skArc(sketch, "E749", {"start": v(169.5, 8.95) * mm, "mid": v(167.9, 7.35) * mm, "end": v(169.5, 5.75) * mm});
            skLineSegment(sketch, "E750", {"start": v(-174.5, 5.75) * mm, "end": v(-169.5, 5.75) * mm});
            skArc(sketch, "E751", {"start": v(-174.5, 8.95) * mm, "mid": v(-176.1, 7.35) * mm, "end": v(-174.5, 5.75) * mm});
            skLineSegment(sketch, "E752", {"start": v(-169.5, 8.95) * mm, "end": v(-174.5, 8.95) * mm});
            skArc(sketch, "E753", {"start": v(-169.5, 5.75) * mm, "mid": v(-167.9, 7.35) * mm, "end": v(-169.5, 8.95) * mm});
            skLineSegment(sketch, "E754", {"start": v(-128, -120.15) * mm, "end": v(-128, -112.15) * mm});
            skArc(sketch, "E755", {"start": v(-136, -120.15) * mm, "mid": v(-132, -124.15) * mm, "end": v(-128, -120.15) * mm});
            skLineSegment(sketch, "E756", {"start": v(-136, -112.15) * mm, "end": v(-136, -120.15) * mm});
            skArc(sketch, "E757", {"start": v(-128, -112.15) * mm, "mid": v(-132, -108.15) * mm, "end": v(-136, -112.15) * mm});
            skLineSegment(sketch, "E758", {"start": v(-161, 75.98) * mm, "end": v(-138, 75.98) * mm});
            skArc(sketch, "E759", {"start": v(-165, 79.98) * mm, "mid": v(-163.83, 77.15) * mm, "end": v(-161, 75.98) * mm});
            skLineSegment(sketch, "E760", {"start": v(-165, 118.85) * mm, "end": v(-165, 79.98) * mm});
            skLineSegment(sketch, "E761", {"start": v(-164, 118.85) * mm, "end": v(-165, 118.85) * mm});
            skArc(sketch, "E762", {"start": v(-162, 116.85) * mm, "mid": v(-162.59, 118.26) * mm, "end": v(-164, 118.85) * mm});
            skLineSegment(sketch, "E763", {"start": v(-162, 79.98) * mm, "end": v(-162, 116.85) * mm});
            skArc(sketch, "E764", {"start": v(-162, 79.98) * mm, "mid": v(-161.7, 79.27) * mm, "end": v(-161, 78.98) * mm});
            skLineSegment(sketch, "E765", {"start": v(-138, 78.98) * mm, "end": v(-161, 78.98) * mm});
            skArc(sketch, "E766", {"start": v(-138, 78.98) * mm, "mid": v(-137.3, 79.27) * mm, "end": v(-137, 79.98) * mm});
            skLineSegment(sketch, "E767", {"start": v(-137, 93.98) * mm, "end": v(-137, 79.98) * mm});
            skLineSegment(sketch, "E768", {"start": v(-136, 93.98) * mm, "end": v(-137, 93.98) * mm});
            skArc(sketch, "E769", {"start": v(-134, 91.98) * mm, "mid": v(-134.59, 93.4) * mm, "end": v(-136, 93.98) * mm});
            skLineSegment(sketch, "E770", {"start": v(-134, 79.98) * mm, "end": v(-134, 91.98) * mm});
            skArc(sketch, "E771", {"start": v(-138, 75.98) * mm, "mid": v(-135.17, 77.15) * mm, "end": v(-134, 79.98) * mm});
            skLineSegment(sketch, "E772", {"start": v(-159, 96.98) * mm, "end": v(-159, 84.98) * mm});
            skArc(sketch, "E773", {"start": v(-155, 100.98) * mm, "mid": v(-157.83, 99.8) * mm, "end": v(-159, 96.98) * mm});
            skLineSegment(sketch, "E774", {"start": v(-132, 100.98) * mm, "end": v(-155, 100.98) * mm});
            skArc(sketch, "E775", {"start": v(-128, 96.98) * mm, "mid": v(-129.17, 99.8) * mm, "end": v(-132, 100.98) * mm});
            skLineSegment(sketch, "E776", {"start": v(-128, 62.98) * mm, "end": v(-128, 96.98) * mm});
            skArc(sketch, "E777", {"start": v(-132, 58.98) * mm, "mid": v(-129.17, 60.15) * mm, "end": v(-128, 62.98) * mm});
            skLineSegment(sketch, "E778", {"start": v(-151, 58.98) * mm, "end": v(-132, 58.98) * mm});
            skArc(sketch, "E779", {"start": v(-153, 60.98) * mm, "mid": v(-152.41, 59.57) * mm, "end": v(-151, 58.98) * mm});
            skLineSegment(sketch, "E780", {"start": v(-153, 61.98) * mm, "end": v(-153, 60.98) * mm});
            skLineSegment(sketch, "E781", {"start": v(-132, 61.98) * mm, "end": v(-153, 61.98) * mm});
            skArc(sketch, "E782", {"start": v(-132, 61.98) * mm, "mid": v(-131.3, 62.27) * mm, "end": v(-131, 62.98) * mm});
            skLineSegment(sketch, "E783", {"start": v(-131, 96.98) * mm, "end": v(-131, 62.98) * mm});
            skArc(sketch, "E784", {"start": v(-131, 96.98) * mm, "mid": v(-131.3, 97.69) * mm, "end": v(-132, 97.98) * mm});
            skLineSegment(sketch, "E785", {"start": v(-155, 97.98) * mm, "end": v(-132, 97.98) * mm});
            skArc(sketch, "E786", {"start": v(-155, 97.98) * mm, "mid": v(-155.7, 97.69) * mm, "end": v(-156, 96.98) * mm});
            skLineSegment(sketch, "E787", {"start": v(-156, 82.98) * mm, "end": v(-156, 96.98) * mm});
            skLineSegment(sketch, "E788", {"start": v(-157, 82.98) * mm, "end": v(-156, 82.98) * mm});
            skArc(sketch, "E789", {"start": v(-159, 84.98) * mm, "mid": v(-158.41, 83.57) * mm, "end": v(-157, 82.98) * mm});
            skLineSegment(sketch, "E790", {"start": v(-153, 91.98) * mm, "end": v(-144, 91.98) * mm});
            skArc(sketch, "E791", {"start": v(-150, 94.98) * mm, "mid": v(-152.12, 94.1) * mm, "end": v(-153, 91.98) * mm});
            skLineSegment(sketch, "E792", {"start": v(-143, 94.98) * mm, "end": v(-150, 94.98) * mm});
            skArc(sketch, "E793", {"start": v(-140, 91.98) * mm, "mid": v(-140.88, 94.1) * mm, "end": v(-143, 94.98) * mm});
            skLineSegment(sketch, "E794", {"start": v(-140, 86.98) * mm, "end": v(-140, 91.98) * mm});
            skLineSegment(sketch, "E795", {"start": v(-143, 86.98) * mm, "end": v(-140, 86.98) * mm});
            skLineSegment(sketch, "E796", {"start": v(-143, 90.98) * mm, "end": v(-143, 86.98) * mm});
            skArc(sketch, "E797", {"start": v(-143, 90.98) * mm, "mid": v(-143.3, 91.69) * mm, "end": v(-144, 91.98) * mm});
            skLineSegment(sketch, "E798", {"start": v(-140, 84.98) * mm, "end": v(-149, 84.98) * mm});
            skArc(sketch, "E799", {"start": v(-143, 81.98) * mm, "mid": v(-140.88, 82.86) * mm, "end": v(-140, 84.98) * mm});
            skLineSegment(sketch, "E800", {"start": v(-150, 81.98) * mm, "end": v(-143, 81.98) * mm});
            skArc(sketch, "E801", {"start": v(-153, 84.98) * mm, "mid": v(-152.12, 82.86) * mm, "end": v(-150, 81.98) * mm});
            skLineSegment(sketch, "E802", {"start": v(-153, 89.98) * mm, "end": v(-153, 84.98) * mm});
            skLineSegment(sketch, "E803", {"start": v(-150, 89.98) * mm, "end": v(-153, 89.98) * mm});
            skLineSegment(sketch, "E804", {"start": v(-150, 85.98) * mm, "end": v(-150, 89.98) * mm});
            skArc(sketch, "E805", {"start": v(-150, 85.98) * mm, "mid": v(-149.7, 85.27) * mm, "end": v(-149, 84.98) * mm});
            skCircle(sketch, "E806", {"center": v(-80, 158.85) * mm, "radius": 1.6 * mm});
            skCircle(sketch, "E807", {"center": v(80, 158.85) * mm, "radius": 1.6 * mm});
            skCircle(sketch, "E808", {"center": v(180, -171.15) * mm, "radius": 1.6 * mm});
            skLineSegment(sketch, "E809", {"start": v(175.82, 160.75) * mm, "end": v(175.82, 170.75) * mm});
            skLineSegment(sketch, "E810", {"start": v(171.82, 160.75) * mm, "end": v(175.82, 160.75) * mm});
            skLineSegment(sketch, "E811", {"start": v(171.82, 170.75) * mm, "end": v(171.82, 160.75) * mm});
            skLineSegment(sketch, "E812", {"start": v(175.82, 170.75) * mm, "end": v(171.82, 170.75) * mm});
            skLineSegment(sketch, "E813", {"start": v(175.82, 135.75) * mm, "end": v(175.82, 145.75) * mm});
            skLineSegment(sketch, "E814", {"start": v(171.82, 135.75) * mm, "end": v(175.82, 135.75) * mm});
            skLineSegment(sketch, "E815", {"start": v(171.82, 145.75) * mm, "end": v(171.82, 135.75) * mm});
            skLineSegment(sketch, "E816", {"start": v(175.82, 145.75) * mm, "end": v(171.82, 145.75) * mm});
            skSolve(sketch);
        }
        {
            var Q0;
            Q0=qSketchRegion(id+"F0",true);
            extrude(context, id + "F1", {"entities" : qUnion([Q0]), "depth" : 3 * mm, "offsetDistance" : 25 * mm});
        }
    });
